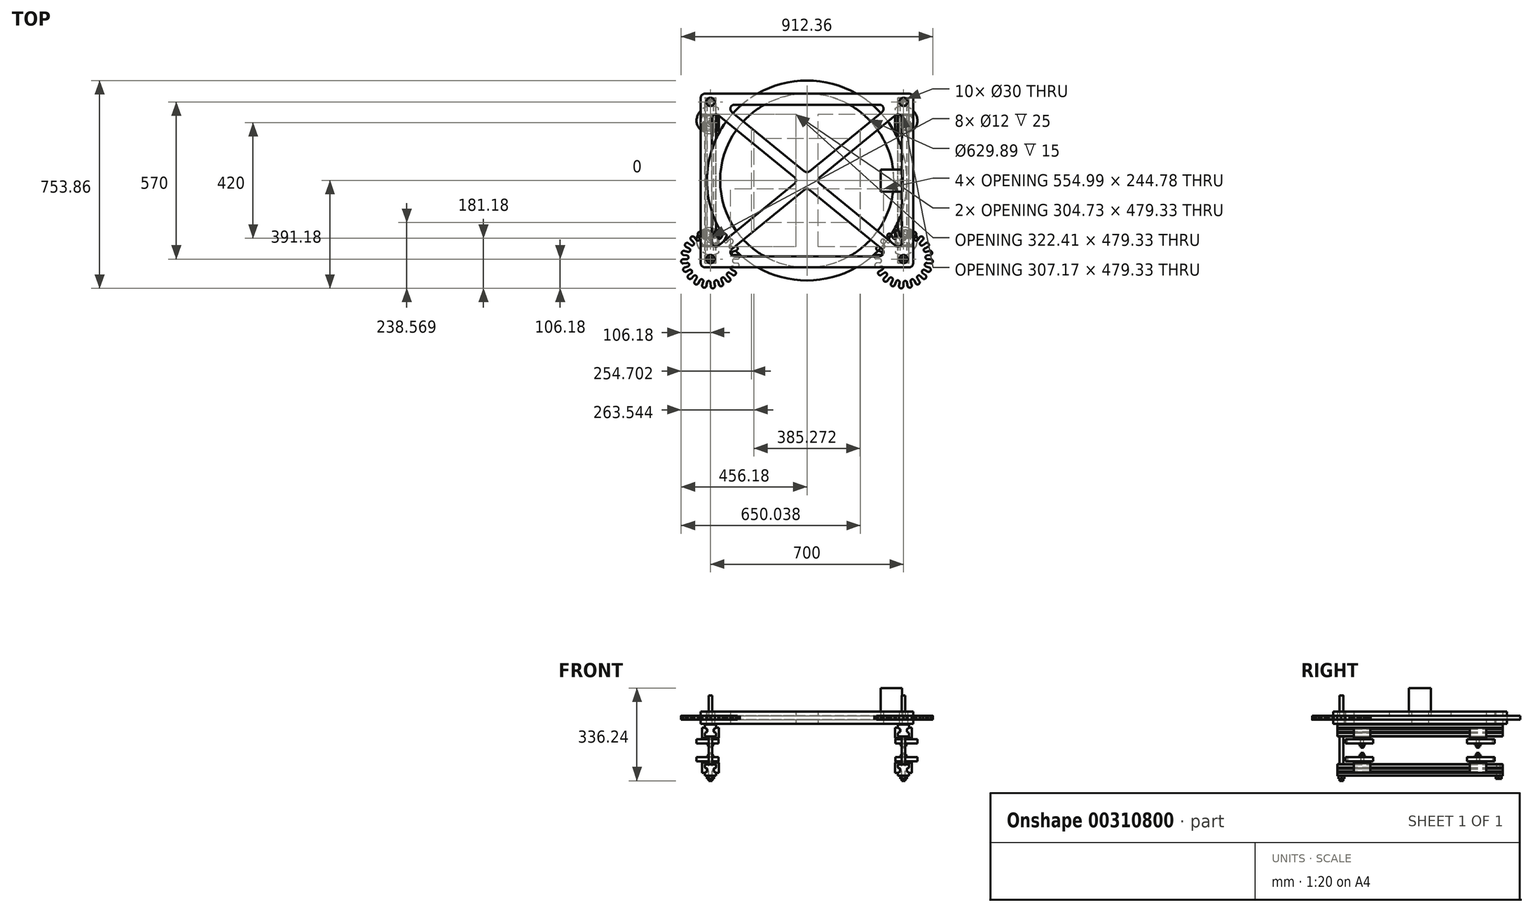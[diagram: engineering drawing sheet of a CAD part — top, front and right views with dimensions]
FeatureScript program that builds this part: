
annotation { "Feature Type Name" : "Feature", "Feature Type Description" : "" }
export const myFeature = defineFeature(function(context is Context, id is Id, definition is map)
    precondition{}
    {
        {
            var Q0;
            Q0=qCreatedBy(makeId("Top.planeOp"),FACE);
            var sketch = newSketch(context, id + "F0", { "sketchPlane" : qUnion([Q0])});
            skLineSegment(sketch, "E0", {"start": v(0, 362.2) * mm, "end": v(0, -359) * mm, "construction": true});
            skLineSegment(sketch, "E1", {"start": v(-350, -300) * mm, "end": v(-350, 300) * mm});
            skLineSegment(sketch, "E2", {"start": v(-645.56, 0) * mm, "end": v(704, 0) * mm, "construction": true});
            skCircle(sketch, "E3", {"center": v(-350, -285) * mm, "radius": 10 * mm});
            skCircle(sketch, "E4.0", {"center": v(-350, -285) * mm, "radius": 6.4 * mm});
            skCircle(sketch, "E5.MirrorC", {"center": v(-350, 285) * mm, "radius": 10 * mm});
            skCircle(sketch, "E6.MirrorC", {"center": v(-350, 285) * mm, "radius": 6.4 * mm});
            skSolve(sketch);
        }
        {
            var Q0;
            Q0=qCreatedBy(makeId("Front.planeOp"),FACE);
            var sketch = newSketch(context, id + "F1", { "sketchPlane" : qUnion([Q0])});
            skPoint(sketch, "E7.0", {"position": v(-350, 0) * mm});
            skLineSegment(sketch, "E8", {"start": v(-350, 0) * mm, "end": v(-330, 0) * mm});
            skLineSegment(sketch, "E9", {"start": v(-330, 0) * mm, "end": v(-330, -12) * mm});
            skLineSegment(sketch, "E10", {"start": v(-330, -12) * mm, "end": v(-338, -16.62) * mm});
            skLineSegment(sketch, "E11", {"start": v(-338, -16.62) * mm, "end": v(-338, -26.62) * mm});
            skLineSegment(sketch, "E12", {"start": v(-338, -26.62) * mm, "end": v(-330, -31.24) * mm});
            skLineSegment(sketch, "E13", {"start": v(-330, -31.24) * mm, "end": v(-330, -41.24) * mm});
            skLineSegment(sketch, "E14", {"start": v(-330, -41.24) * mm, "end": v(-350, -41.24) * mm});
            skLineSegment(sketch, "E15", {"start": v(-350, 0) * mm, "end": v(-350, -46.41) * mm, "construction": true});
            skPoint(sketch, "E16.orphan", {"position": v(-361.17, 0) * mm});
            skLineSegment(sketch, "E17.MirrorCS", {"start": v(-370, -41.24) * mm, "end": v(-350, -41.24) * mm});
            skLineSegment(sketch, "E18.MirrorCS", {"start": v(-370, -31.24) * mm, "end": v(-370, -41.24) * mm});
            skLineSegment(sketch, "E19.MirrorCS", {"start": v(-362, -26.62) * mm, "end": v(-370, -31.24) * mm});
            skLineSegment(sketch, "E20.MirrorCS", {"start": v(-362, -16.62) * mm, "end": v(-362, -26.62) * mm});
            skLineSegment(sketch, "E21.MirrorCS", {"start": v(-370, -12) * mm, "end": v(-362, -16.62) * mm});
            skLineSegment(sketch, "E22.MirrorCS", {"start": v(-370, 0) * mm, "end": v(-370, -12) * mm});
            skLineSegment(sketch, "E23.MirrorCS", {"start": v(-350, 0) * mm, "end": v(-370, 0) * mm});
            skLineSegment(sketch, "E24", {"start": v(0, 0) * mm, "end": v(0, -83.34) * mm, "construction": true});
            skSolve(sketch);
        }
        {
            var Q0;
            Q0 = qSketchRegion(id + "F1", true);
            extrude(context, id + "F2", {"entities" : qUnion([Q0]), "depth" : 600 * mm, "offsetDistance" : 25 * mm, "symmetric" : true});
        }
        {
            var Q0;
            {var subQ0=sQuery(id+"F0.wireOp",EDGE,"E4.0");var subQ1=sQuery(id+"F0.wireOp",EDGE,"E1");var subQ2=makeQuery(id+"F0.imprint","INTERSECT",VERTEX,{"disambiguationData":[OD(0.0)],"derivedFrom":[subQ1,subQ0]});Q0=makeQuery(id+"F0.imprint","IMPRINT",FACE,{"disambiguationData":[TD([[makeQuery(id+"F0.imprint","IMPRINT",EDGE,{"disambiguationData":[TD([[subQ2,-1.0]])],"derivedFrom":subQ1}),1.0]])]});}
            var Q1;
            {var subQ0=sQuery(id+"F0.wireOp",EDGE,"E4.0");var subQ1=sQuery(id+"F0.wireOp",EDGE,"E1");var subQ2=makeQuery(id+"F0.imprint","INTERSECT",VERTEX,{"disambiguationData":[OD(0.0)],"derivedFrom":[subQ1,subQ0]});Q1=makeQuery(id+"F0.imprint","IMPRINT",FACE,{"disambiguationData":[TD([[makeQuery(id+"F0.imprint","IMPRINT",EDGE,{"disambiguationData":[TD([[subQ2,-1.0]])],"derivedFrom":subQ1}),-1.0]])]});}
            var Q2;
            {var subQ0=sQuery(id+"F0.wireOp",EDGE,"E6.MirrorC");var subQ1=sQuery(id+"F0.wireOp",EDGE,"E1");var subQ2=makeQuery(id+"F0.imprint","INTERSECT",VERTEX,{"disambiguationData":[OD(0.0)],"derivedFrom":[subQ1,subQ0]});Q2=makeQuery(id+"F0.imprint","IMPRINT",FACE,{"disambiguationData":[TD([[makeQuery(id+"F0.imprint","IMPRINT",EDGE,{"disambiguationData":[TD([[subQ2,-1.0]])],"derivedFrom":subQ1}),1.0]])]});}
            var Q3;
            {var subQ0=sQuery(id+"F0.wireOp",EDGE,"E6.MirrorC");var subQ1=sQuery(id+"F0.wireOp",EDGE,"E1");var subQ2=makeQuery(id+"F0.imprint","INTERSECT",VERTEX,{"disambiguationData":[OD(0.0)],"derivedFrom":[subQ1,subQ0]});Q3=makeQuery(id+"F0.imprint","IMPRINT",FACE,{"disambiguationData":[TD([[makeQuery(id+"F0.imprint","IMPRINT",EDGE,{"disambiguationData":[TD([[subQ2,-1.0]])],"derivedFrom":subQ1}),-1.0]])]});}
            var Q4;
            {var subQ0=sQuery(id+"F0.wireOp",EDGE,"7edcf58e-238c-42a4-a463-77a39aa3dbbc0.MirrorC");var subQ1=sQuery(id+"F0.wireOp",EDGE,"05d8a813-b1b4-46cf-a819-2d3db73e43fd0.MirrorCS");var subQ2=makeQuery(id+"F0.imprint","INTERSECT",VERTEX,{"disambiguationData":[OD(0.0)],"derivedFrom":[subQ1,subQ0]});Q4=makeQuery(id+"F0.imprint","IMPRINT",FACE,{"disambiguationData":[TD([[makeQuery(id+"F0.imprint","IMPRINT",EDGE,{"disambiguationData":[TD([[subQ2,-1.0]])],"derivedFrom":subQ1}),-1.0]])]});}
            var Q5;
            {var subQ0=sQuery(id+"F0.wireOp",EDGE,"7edcf58e-238c-42a4-a463-77a39aa3dbbc0.MirrorC");var subQ1=sQuery(id+"F0.wireOp",EDGE,"05d8a813-b1b4-46cf-a819-2d3db73e43fd0.MirrorCS");var subQ2=makeQuery(id+"F0.imprint","INTERSECT",VERTEX,{"disambiguationData":[OD(0.0)],"derivedFrom":[subQ1,subQ0]});Q5=makeQuery(id+"F0.imprint","IMPRINT",FACE,{"disambiguationData":[TD([[makeQuery(id+"F0.imprint","IMPRINT",EDGE,{"disambiguationData":[TD([[subQ2,-1.0]])],"derivedFrom":subQ1}),1.0]])]});}
            var Q6;
            {var subQ0=sQuery(id+"F0.wireOp",EDGE,"8badf943-bae0-46a3-bb4d-9388d6aff6ef0.MirrorC");var subQ1=sQuery(id+"F0.wireOp",EDGE,"05d8a813-b1b4-46cf-a819-2d3db73e43fd0.MirrorCS");var subQ2=makeQuery(id+"F0.imprint","INTERSECT",VERTEX,{"disambiguationData":[OD(0.0)],"derivedFrom":[subQ1,subQ0]});Q6=makeQuery(id+"F0.imprint","IMPRINT",FACE,{"disambiguationData":[TD([[makeQuery(id+"F0.imprint","IMPRINT",EDGE,{"disambiguationData":[TD([[subQ2,-1.0]])],"derivedFrom":subQ1}),-1.0]])]});}
            var Q7;
            {var subQ0=sQuery(id+"F0.wireOp",EDGE,"8badf943-bae0-46a3-bb4d-9388d6aff6ef0.MirrorC");var subQ1=sQuery(id+"F0.wireOp",EDGE,"05d8a813-b1b4-46cf-a819-2d3db73e43fd0.MirrorCS");var subQ2=makeQuery(id+"F0.imprint","INTERSECT",VERTEX,{"disambiguationData":[OD(0.0)],"derivedFrom":[subQ1,subQ0]});Q7=makeQuery(id+"F0.imprint","IMPRINT",FACE,{"disambiguationData":[TD([[makeQuery(id+"F0.imprint","IMPRINT",EDGE,{"disambiguationData":[TD([[subQ2,-1.0]])],"derivedFrom":subQ1}),1.0]])]});}
            extrude(context, id + "F3", {"entities" : qUnion([Q0, Q1, Q2, Q3, Q4, Q5, Q6, Q7]), "operationType" : NewBodyOperationType.REMOVE, "endBound" : BoundingType.UP_TO_NEXT, "oppositeDirection" : true, "depth" : 25 * mm, "offsetDistance" : 25 * mm});
        }
        {
            var Q0;
            Q0=makeQuery(id+"F2.opExtrude","CAP_FACE",FACE,{"disambiguationData":[OSD([sQuery(id+"F1.wireOp",EDGE,"E8"),sQuery(id+"F1.wireOp",EDGE,"E9"),sQuery(id+"F1.wireOp",EDGE,"E10"),sQuery(id+"F1.wireOp",EDGE,"E11"),sQuery(id+"F1.wireOp",EDGE,"E12"),sQuery(id+"F1.wireOp",EDGE,"E13"),sQuery(id+"F1.wireOp",EDGE,"E14"),sQuery(id+"F1.wireOp",EDGE,"E17.MirrorCS"),sQuery(id+"F1.wireOp",EDGE,"E18.MirrorCS"),sQuery(id+"F1.wireOp",EDGE,"E19.MirrorCS"),sQuery(id+"F1.wireOp",EDGE,"E20.MirrorCS"),sQuery(id+"F1.wireOp",EDGE,"E21.MirrorCS"),sQuery(id+"F1.wireOp",EDGE,"E22.MirrorCS"),sQuery(id+"F1.wireOp",EDGE,"E23.MirrorCS")])],"isStart":false});
            cPlane(context, id + "F4", {"entities" : qUnion([Q0]), "cplaneType" : CPlaneType.OFFSET, "offset" : 60 * mm, "oppositeDirection" : true, "width" : 150 * mm, "height" : 150 * mm});
        }
        {
            var Q0;
            Q0=qCreatedBy(id+"F4.planeOp",FACE);
            var sketch = newSketch(context, id + "F5", { "sketchPlane" : qUnion([Q0])});
            skLineSegment(sketch, "E25.0.1", {"start": v(-370, 0) * mm, "end": v(-370, -12) * mm, "construction": true});
            skLineSegment(sketch, "E25.0.2", {"start": v(-370, -12) * mm, "end": v(-362, -16.62) * mm, "construction": true});
            skLineSegment(sketch, "E25.0.3", {"start": v(-362, -16.62) * mm, "end": v(-362, -26.62) * mm, "construction": true});
            skLineSegment(sketch, "E25.0.4", {"start": v(-362, -26.62) * mm, "end": v(-370, -31.24) * mm, "construction": true});
            skLineSegment(sketch, "E25.0.5", {"start": v(-370, -31.24) * mm, "end": v(-370, -41.24) * mm, "construction": true});
            skLineSegment(sketch, "E25.0.7", {"start": v(-330, -41.24) * mm, "end": v(-330, -31.24) * mm, "construction": true});
            skLineSegment(sketch, "E25.0.8", {"start": v(-330, -31.24) * mm, "end": v(-338, -26.62) * mm, "construction": true});
            skLineSegment(sketch, "E25.0.9", {"start": v(-338, -26.62) * mm, "end": v(-338, -16.62) * mm, "construction": true});
            skLineSegment(sketch, "E25.0.10", {"start": v(-338, -16.62) * mm, "end": v(-330, -12) * mm, "construction": true});
            skLineSegment(sketch, "E25.0.11", {"start": v(-330, -12) * mm, "end": v(-330, 0) * mm, "construction": true});
            skLineSegment(sketch, "E26.0", {"start": v(-329.5, -12.29) * mm, "end": v(-329.5, 0.5) * mm});
            skLineSegment(sketch, "E26.2", {"start": v(-329, -31.24) * mm, "end": v(-337.5, -26.33) * mm});
            skLineSegment(sketch, "E26.3", {"start": v(-337.5, -26.33) * mm, "end": v(-337.5, -16.9) * mm});
            skLineSegment(sketch, "E26.4", {"start": v(-337.5, -16.9) * mm, "end": v(-329.5, -12.29) * mm});
            skLineSegment(sketch, "E27", {"start": v(-370, 0) * mm, "end": v(-330, 0) * mm, "construction": true});
            skLineSegment(sketch, "E28.1", {"start": v(-362.5, -26.33) * mm, "end": v(-371, -31.24) * mm});
            skLineSegment(sketch, "E28.2", {"start": v(-370.5, 0.5) * mm, "end": v(-329.5, 0.5) * mm});
            skLineSegment(sketch, "E28.3", {"start": v(-370.5, 0.5) * mm, "end": v(-370.5, -12.29) * mm});
            skLineSegment(sketch, "E28.4", {"start": v(-370.5, -12.29) * mm, "end": v(-362.5, -16.9) * mm});
            skLineSegment(sketch, "E28.5", {"start": v(-362.5, -16.9) * mm, "end": v(-362.5, -26.33) * mm});
            skLineSegment(sketch, "E29", {"start": v(-371, -31.24) * mm, "end": v(-380.5, -31.24) * mm});
            skLineSegment(sketch, "E30", {"start": v(-380.5, -31.24) * mm, "end": v(-380.5, 10.5) * mm});
            skLineSegment(sketch, "E31", {"start": v(-319.5, 10.5) * mm, "end": v(-319.5, -31.24) * mm});
            skLineSegment(sketch, "E32", {"start": v(-319.5, -31.24) * mm, "end": v(-329, -31.24) * mm});
            skLineSegment(sketch, "E33", {"start": v(-380.5, 10.5) * mm, "end": v(-319.5, 10.5) * mm});
            skSolve(sketch);
        }
        {
            var Q0;
            Q0 = qSketchRegion(id + "F5", true);
            extrude(context, id + "F6", {"entities" : qUnion([Q0]), "oppositeDirection" : true, "depth" : 60 * mm, "offsetDistance" : 25 * mm});
        }
        {
            var Q0;
            Q0=makeQuery(id+"F2.opExtrude","SWEPT_EDGE",EDGE,{"disambiguationData":[OSD([sQuery(id+"F1.wireOp",EDGE,"E8"),sQuery(id+"F1.wireOp",EDGE,"E9")])]});
            var Q1;
            Q1=makeQuery(id+"F2.opExtrude","SWEPT_FACE",FACE,{"disambiguationData":[OSD([sQuery(id+"F1.wireOp",EDGE,"E8"),sQuery(id+"F1.wireOp",EDGE,"E23.MirrorCS")])]});
            var Q2;
            Q2=makeQuery(id+"F2.opExtrude","SWEPT_EDGE",EDGE,{"disambiguationData":[OSD([sQuery(id+"F1.wireOp",EDGE,"aa46a0b6-513b-4986-81cd-16920383a29b9.MirrorCS"),sQuery(id+"F1.wireOp",EDGE,"aa46a0b6-513b-4986-81cd-16920383a29b11.MirrorCS")])]});
            var Q3;
            Q3=makeQuery(id+"F2.opExtrude","SWEPT_FACE",FACE,{"disambiguationData":[OSD([sQuery(id+"F1.wireOp",EDGE,"aa46a0b6-513b-4986-81cd-16920383a29b10.MirrorCS"),sQuery(id+"F1.wireOp",EDGE,"aa46a0b6-513b-4986-81cd-16920383a29b11.MirrorCS")])]});
            chamfer(context, id + "F7", {"entities" : qUnion([Q0, Q1, Q2, Q3]), "width" : 1 * mm, "tangentPropagation" : true});
        }
        {
            var Q0;
            Q0=makeQuery(id+"F6.opExtrude","SWEPT_EDGE",EDGE,{"disambiguationData":[OSD([sQuery(id+"F5.wireOp",EDGE,"E28.2"),sQuery(id+"F5.wireOp",EDGE,"E28.3")])]});
            var Q1;
            Q1=makeQuery(id+"F6.opExtrude","SWEPT_EDGE",EDGE,{"disambiguationData":[OSD([sQuery(id+"F5.wireOp",EDGE,"E26.0"),sQuery(id+"F5.wireOp",EDGE,"E28.2")])]});
            chamfer(context, id + "F8", {"entities" : qUnion([Q0, Q1]), "width" : 1 * mm, "tangentPropagation" : true});
        }
        {
            var Q0;
            Q0=makeQuery(id+"F6.opExtrude","CAP_EDGE",EDGE,{"disambiguationData":[OSD([sQuery(id+"F5.wireOp",EDGE,"E33")])],"isStart":true});
            var Q1;
            Q1=makeQuery(id+"F6.opExtrude","SWEPT_FACE",FACE,{"disambiguationData":[OSD([sQuery(id+"F5.wireOp",EDGE,"E33")])]});
            chamfer(context, id + "F9", {"entities" : qUnion([Q0, Q1]), "width" : 5 * mm, "tangentPropagation" : true});
        }
        {
            var Q0;
            Q0=makeQuery(id+"F6.opExtrude","SWEPT_FACE",FACE,{"disambiguationData":[OSD([sQuery(id+"F5.wireOp",EDGE,"E33")])]});
            var sketch = newSketch(context, id + "F10", { "sketchPlane" : qUnion([Q0])});
            skCircle(sketch, "E34", {"center": v(-350, -210) * mm, "radius": 5 * mm});
            skPoint(sketch, "E34.centerSnap0", {"position": v(-324.5, -210) * mm});
            skPoint(sketch, "E34.centerSnap1", {"position": v(-350, -235) * mm});
            skCircle(sketch, "E35.0", {"center": v(-350, -210) * mm, "radius": 6 * mm});
            skCircle(sketch, "E36", {"center": v(-350, -210) * mm, "radius": 29 * mm, "construction": true});
            skArc(sketch, "E37", {"start": v(-350, -270) * mm, "mid": v(-335.03, -268.1) * mm, "end": v(-321, -262.53) * mm});
            skLineSegment(sketch, "E38", {"start": v(-350, -270) * mm, "end": v(-350, -150) * mm, "construction": true});
            skLineSegment(sketch, "E39", {"start": v(-321, -210) * mm, "end": v(-410, -210) * mm, "construction": true});
            skFitSpline(sketch, "E40", {"points": [v(-350, -270) * mm, v(-400, -210) * mm, v(-350, -170) * mm, v(-321, -210) * mm], "startDerivative": vector(-250.58, 0) * mm, "endDerivative": vector(0, -219.6) * mm});
            skLineSegment(sketch, "E41", {"start": v(-321, -210) * mm, "end": v(-321, -262.53) * mm});
            skLineSegment(sketch, "E42", {"start": v(-350, -270) * mm, "end": v(-312.43, -270) * mm, "construction": true});
            skSolve(sketch);
        }
        {
            var Q0;
            Q0=makeQuery(id+"F10.imprint","IMPRINT",FACE,{"disambiguationData":[TD([[makeQuery(id+"F10.imprint","IMPRINT",EDGE,{"derivedFrom":sQuery(id+"F10.wireOp",EDGE,"E34")}),1.0]])]});
            var Q1;
            Q1=sQuery(id+"F10.wireOp",EDGE,"E34");
            extrude(context, id + "F11", {"entities" : qUnion([Q0]), "operationType" : NewBodyOperationType.ADD, "surfaceEntities" : qUnion([Q1]), "depth" : 30 * mm, "offsetDistance" : 25 * mm});
        }
        {
            var Q0;
            {var subQ6=sQuery(id+"F10.wireOp",EDGE,"E37");Q0=makeQuery(id+"F10.imprint","IMPRINT",FACE,{"disambiguationData":[TD([[makeQuery(id+"F10.imprint","IMPRINT",EDGE,{"derivedFrom":subQ6}),1.0]])]});}
            var Q1;
            Q1=makeQuery(id+"F10.imprint","IMPRINT",FACE,{"disambiguationData":[TD([[makeQuery(id+"F10.imprint","IMPRINT",EDGE,{"derivedFrom":sQuery(id+"F10.wireOp",EDGE,"E35.0")}),-1.0]])]});
            extrude(context, id + "F12", {"entities" : qUnion([Q0, Q1]), "depth" : 15 * mm, "offsetDistance" : 25 * mm});
        }
        {
            var Q0;
            Q0=makeQuery(id+"F12.opExtrude","CAP_FACE",FACE,{"disambiguationData":[OSD([sQuery(id+"F10.wireOp",EDGE,"E35.0"),sQuery(id+"F10.wireOp",EDGE,"E37"),sQuery(id+"F10.wireOp",EDGE,"E40"),sQuery(id+"F10.wireOp",EDGE,"E41")])],"isStart":false});
            var sketch = newSketch(context, id + "F13", { "sketchPlane" : qUnion([Q0])});
            skCircle(sketch, "E43.0", {"center": v(-350, -210) * mm, "radius": 5 * mm});
            skCircle(sketch, "E44", {"center": v(-350, -210) * mm, "radius": 15 * mm});
            skCircle(sketch, "E45.cCircle", {"center": v(-350, -210) * mm, "radius": 8.06 * mm, "construction": true});
            skLineSegment(sketch, "E45.0", {"start": v(-345.35, -218.06) * mm, "end": v(-354.65, -218.06) * mm});
            skLineSegment(sketch, "E45.1", {"start": v(-354.65, -218.06) * mm, "end": v(-359.3, -210) * mm});
            skLineSegment(sketch, "E45.2", {"start": v(-359.3, -210) * mm, "end": v(-354.65, -201.94) * mm});
            skLineSegment(sketch, "E45.3", {"start": v(-354.65, -201.94) * mm, "end": v(-345.35, -201.94) * mm});
            skLineSegment(sketch, "E45.4", {"start": v(-345.35, -201.94) * mm, "end": v(-340.7, -210) * mm});
            skLineSegment(sketch, "E45.5", {"start": v(-340.7, -210) * mm, "end": v(-345.35, -218.06) * mm});
            skPoint(sketch, "E45.0.midPoint", {"position": v(-350, -218.06) * mm});
            skSolve(sketch);
        }
        {
            var Q0;
            Q0=makeQuery(id+"F13.imprint","IMPRINT",FACE,{"disambiguationData":[TD([[makeQuery(id+"F13.imprint","IMPRINT",EDGE,{"derivedFrom":sQuery(id+"F13.wireOp",EDGE,"E44")}),1.0]])]});
            var Q1;
            Q1=makeQuery(id+"F13.imprint","IMPRINT",FACE,{"disambiguationData":[TD([[makeQuery(id+"F13.imprint","IMPRINT",EDGE,{"derivedFrom":sQuery(id+"F13.wireOp",EDGE,"E45.0")}),-1.0]])]});
            extrude(context, id + "F14", {"entities" : qUnion([Q0, Q1]), "depth" : 2 * mm, "offsetDistance" : 25 * mm});
        }
        {
            var Q0;
            Q0=makeQuery(id+"F13.imprint","IMPRINT",FACE,{"disambiguationData":[TD([[makeQuery(id+"F13.imprint","IMPRINT",EDGE,{"derivedFrom":sQuery(id+"F13.wireOp",EDGE,"E45.0")}),-1.0]])]});
            extrude(context, id + "F15", {"entities" : qUnion([Q0]), "depth" : 10 * mm, "offsetDistance" : 25 * mm});
        }
        {
            var Q0;
            {var subQ0=sQuery(id+"F0.wireOp",EDGE,"E3");var subQ1=sQuery(id+"F0.wireOp",EDGE,"E1");var subQ2=makeQuery(id+"F0.imprint","INTERSECT",VERTEX,{"disambiguationData":[OD(0.0)],"derivedFrom":[subQ1,subQ0]});Q0=makeQuery(id+"F0.imprint","IMPRINT",FACE,{"disambiguationData":[TD([[makeQuery(id+"F0.imprint","IMPRINT",EDGE,{"disambiguationData":[TD([[subQ2,-1.0]])],"derivedFrom":subQ1}),1.0]])]});}
            var Q1;
            {var subQ0=sQuery(id+"F0.wireOp",EDGE,"E3");var subQ1=sQuery(id+"F0.wireOp",EDGE,"E1");var subQ2=makeQuery(id+"F0.imprint","INTERSECT",VERTEX,{"disambiguationData":[OD(0.0)],"derivedFrom":[subQ1,subQ0]});Q1=makeQuery(id+"F0.imprint","IMPRINT",FACE,{"disambiguationData":[TD([[makeQuery(id+"F0.imprint","IMPRINT",EDGE,{"disambiguationData":[TD([[subQ2,-1.0]])],"derivedFrom":subQ1}),-1.0]])]});}
            var Q2;
            {var subQ0=sQuery(id+"F0.wireOp",EDGE,"E4.0");var subQ1=sQuery(id+"F0.wireOp",EDGE,"E1");var subQ2=makeQuery(id+"F0.imprint","INTERSECT",VERTEX,{"disambiguationData":[OD(0.0)],"derivedFrom":[subQ1,subQ0]});Q2=makeQuery(id+"F0.imprint","IMPRINT",FACE,{"disambiguationData":[TD([[makeQuery(id+"F0.imprint","IMPRINT",EDGE,{"disambiguationData":[TD([[subQ2,-1.0]])],"derivedFrom":subQ1}),1.0]])]});}
            var Q3;
            {var subQ0=sQuery(id+"F0.wireOp",EDGE,"E4.0");var subQ1=sQuery(id+"F0.wireOp",EDGE,"E1");var subQ2=makeQuery(id+"F0.imprint","INTERSECT",VERTEX,{"disambiguationData":[OD(0.0)],"derivedFrom":[subQ1,subQ0]});Q3=makeQuery(id+"F0.imprint","IMPRINT",FACE,{"disambiguationData":[TD([[makeQuery(id+"F0.imprint","IMPRINT",EDGE,{"disambiguationData":[TD([[subQ2,-1.0]])],"derivedFrom":subQ1}),-1.0]])]});}
            extrude(context, id + "F16", {"entities" : qUnion([Q0, Q1, Q2, Q3]), "depth" : 250 * mm, "offsetDistance" : 25 * mm});
        }
        {
            var Q0;
            {var subQ0=sQuery(id+"F0.wireOp",EDGE,"E4.0");var subQ1=sQuery(id+"F0.wireOp",EDGE,"E1");var subQ2=makeQuery(id+"F0.imprint","INTERSECT",VERTEX,{"disambiguationData":[OD(0.0)],"derivedFrom":[subQ1,subQ0]});Q0=makeQuery(id+"F0.imprint","IMPRINT",FACE,{"disambiguationData":[TD([[makeQuery(id+"F0.imprint","IMPRINT",EDGE,{"disambiguationData":[TD([[subQ2,-1.0]])],"derivedFrom":subQ1}),1.0]])]});}
            var Q1;
            {var subQ0=sQuery(id+"F0.wireOp",EDGE,"E4.0");var subQ1=sQuery(id+"F0.wireOp",EDGE,"E1");var subQ2=makeQuery(id+"F0.imprint","INTERSECT",VERTEX,{"disambiguationData":[OD(0.0)],"derivedFrom":[subQ1,subQ0]});Q1=makeQuery(id+"F0.imprint","IMPRINT",FACE,{"disambiguationData":[TD([[makeQuery(id+"F0.imprint","IMPRINT",EDGE,{"disambiguationData":[TD([[subQ2,-1.0]])],"derivedFrom":subQ1}),-1.0]])]});}
            extrude(context, id + "F17", {"entities" : qUnion([Q0, Q1]), "operationType" : NewBodyOperationType.ADD, "oppositeDirection" : true, "depth" : 60 * mm, "offsetDistance" : 25 * mm});
        }
        {
            var Q0;
            Q0=makeQuery(id+"F2.opExtrude","SWEPT_FACE",FACE,{"disambiguationData":[OSD([sQuery(id+"F1.wireOp",EDGE,"E14"),sQuery(id+"F1.wireOp",EDGE,"E17.MirrorCS")])]});
            var sketch = newSketch(context, id + "F18", { "sketchPlane" : qUnion([Q0])});
            skCircle(sketch, "E46", {"center": v(-350, 285) * mm, "radius": 15 * mm});
            skCircle(sketch, "E47.cCircle", {"center": v(-350, 285) * mm, "radius": 10.5 * mm, "construction": true});
            skLineSegment(sketch, "E47.0", {"start": v(-356.06, 295.5) * mm, "end": v(-343.94, 295.5) * mm});
            skLineSegment(sketch, "E47.1", {"start": v(-343.94, 295.5) * mm, "end": v(-337.87, 285) * mm});
            skLineSegment(sketch, "E47.2", {"start": v(-337.87, 285) * mm, "end": v(-343.94, 274.5) * mm});
            skLineSegment(sketch, "E47.3", {"start": v(-343.94, 274.5) * mm, "end": v(-356.06, 274.5) * mm});
            skLineSegment(sketch, "E47.4", {"start": v(-356.06, 274.5) * mm, "end": v(-362.13, 285) * mm});
            skLineSegment(sketch, "E47.5", {"start": v(-362.13, 285) * mm, "end": v(-356.06, 295.5) * mm});
            skPoint(sketch, "E47.0.midPoint", {"position": v(-350, 295.5) * mm});
            skSolve(sketch);
        }
        {
            var Q0;
            Q0=makeQuery(id+"F18.imprint","IMPRINT",FACE,{"disambiguationData":[TD([[makeQuery(id+"F18.imprint","IMPRINT",EDGE,{"derivedFrom":sQuery(id+"F18.wireOp",EDGE,"E47.0")}),-1.0]])]});
            extrude(context, id + "F19", {"entities" : qUnion([Q0]), "depth" : 12 * mm, "offsetDistance" : 25 * mm});
        }
        {
            var Q0;
            Q0=makeQuery(id+"F18.imprint","IMPRINT",FACE,{"disambiguationData":[TD([[makeQuery(id+"F18.imprint","IMPRINT",EDGE,{"derivedFrom":sQuery(id+"F18.wireOp",EDGE,"E46")}),1.0]])]});
            extrude(context, id + "F20", {"entities" : qUnion([Q0]), "depth" : 2 * mm, "offsetDistance" : 25 * mm});
        }
        {
            var Q0;
            Q0=makeQuery(id+"F20.opExtrude","SWEPT_BODY",BODY,{"disambiguationData":[OSD([sQuery(id+"F18.wireOp",EDGE,"E46"),sQuery(id+"F18.wireOp",EDGE,"E47.0"),sQuery(id+"F18.wireOp",EDGE,"E47.1"),sQuery(id+"F18.wireOp",EDGE,"E47.2"),sQuery(id+"F18.wireOp",EDGE,"E47.3"),sQuery(id+"F18.wireOp",EDGE,"E47.4"),sQuery(id+"F18.wireOp",EDGE,"E47.5")])]});
            var Q1;
            Q1=makeQuery(id+"F19.opExtrude","SWEPT_BODY",BODY,{"disambiguationData":[OSD([sQuery(id+"F0.wireOp",EDGE,"E4.0"),sQuery(id+"F1.wireOp",EDGE,"E14"),sQuery(id+"F1.wireOp",EDGE,"E17.MirrorCS"),sQuery(id+"F18.wireOp",EDGE,"E47.0"),sQuery(id+"F18.wireOp",EDGE,"E47.1"),sQuery(id+"F18.wireOp",EDGE,"E47.2"),sQuery(id+"F18.wireOp",EDGE,"E47.3"),sQuery(id+"F18.wireOp",EDGE,"E47.4"),sQuery(id+"F18.wireOp",EDGE,"E47.5")])]});
            var Q2;
            Q2=makeQuery(id+"F16.opExtrude","SWEPT_BODY",BODY,{"disambiguationData":[OSD([sQuery(id+"F0.wireOp",EDGE,"E3")])]});
            var Q3;
            Q3=makeQuery(id+"F15.opExtrude","SWEPT_BODY",BODY,{"disambiguationData":[OSD([sQuery(id+"F10.wireOp",EDGE,"E35.0"),sQuery(id+"F13.wireOp",EDGE,"E45.0"),sQuery(id+"F13.wireOp",EDGE,"E45.1"),sQuery(id+"F13.wireOp",EDGE,"E45.2"),sQuery(id+"F13.wireOp",EDGE,"E45.3"),sQuery(id+"F13.wireOp",EDGE,"E45.4"),sQuery(id+"F13.wireOp",EDGE,"E45.5")])]});
            var Q4;
            Q4=makeQuery(id+"F14.opExtrude","SWEPT_BODY",BODY,{"disambiguationData":[OSD([sQuery(id+"F10.wireOp",EDGE,"E35.0"),sQuery(id+"F13.wireOp",EDGE,"E44")])]});
            var Q5;
            Q5=makeQuery(id+"F12.opExtrude","SWEPT_BODY",BODY,{"disambiguationData":[OSD([sQuery(id+"F10.wireOp",EDGE,"E35.0"),sQuery(id+"F10.wireOp",EDGE,"E37"),sQuery(id+"F10.wireOp",EDGE,"E40"),sQuery(id+"F10.wireOp",EDGE,"E41")])]});
            var Q6;
            Q6=makeQuery(id+"F6.opExtrude","SWEPT_BODY",BODY,{"disambiguationData":[OSD([sQuery(id+"F5.wireOp",EDGE,"E26.0"),sQuery(id+"F5.wireOp",EDGE,"E26.2"),sQuery(id+"F5.wireOp",EDGE,"E26.3"),sQuery(id+"F5.wireOp",EDGE,"E26.4"),sQuery(id+"F5.wireOp",EDGE,"E28.1"),sQuery(id+"F5.wireOp",EDGE,"E28.2"),sQuery(id+"F5.wireOp",EDGE,"E28.3"),sQuery(id+"F5.wireOp",EDGE,"E28.4"),sQuery(id+"F5.wireOp",EDGE,"E28.5"),sQuery(id+"F5.wireOp",EDGE,"E29"),sQuery(id+"F5.wireOp",EDGE,"E30"),sQuery(id+"F5.wireOp",EDGE,"E31"),sQuery(id+"F5.wireOp",EDGE,"E32"),sQuery(id+"F5.wireOp",EDGE,"E33")])]});
            var Q7;
            Q7=qCreatedBy(makeId("Front.planeOp"),FACE);
            mirror(context, id + "F21", {"operationType" : NewBodyOperationType.ADD, "entities" : qUnion([Q0, Q1, Q2, Q3, Q4, Q5, Q6]), "mirrorPlane" : qUnion([Q7])});
        }
        {
            var Q0;
            Q0=makeQuery(id+"F6.opExtrude","SWEPT_BODY",BODY,{"disambiguationData":[OSD([sQuery(id+"F5.wireOp",EDGE,"E26.0"),sQuery(id+"F5.wireOp",EDGE,"E26.2"),sQuery(id+"F5.wireOp",EDGE,"E26.3"),sQuery(id+"F5.wireOp",EDGE,"E26.4"),sQuery(id+"F5.wireOp",EDGE,"E28.1"),sQuery(id+"F5.wireOp",EDGE,"E28.2"),sQuery(id+"F5.wireOp",EDGE,"E28.3"),sQuery(id+"F5.wireOp",EDGE,"E28.4"),sQuery(id+"F5.wireOp",EDGE,"E28.5"),sQuery(id+"F5.wireOp",EDGE,"E29"),sQuery(id+"F5.wireOp",EDGE,"E30"),sQuery(id+"F5.wireOp",EDGE,"E31"),sQuery(id+"F5.wireOp",EDGE,"E32"),sQuery(id+"F5.wireOp",EDGE,"E33")])]});
            var Q1;
            Q1=makeQuery(id+"F21.opPattern","COPY",BODY,{"derivedFrom":makeQuery(id+"F6.opExtrude","SWEPT_BODY",BODY,{"disambiguationData":[OSD([sQuery(id+"F5.wireOp",EDGE,"E26.0"),sQuery(id+"F5.wireOp",EDGE,"E26.2"),sQuery(id+"F5.wireOp",EDGE,"E26.3"),sQuery(id+"F5.wireOp",EDGE,"E26.4"),sQuery(id+"F5.wireOp",EDGE,"E28.1"),sQuery(id+"F5.wireOp",EDGE,"E28.2"),sQuery(id+"F5.wireOp",EDGE,"E28.3"),sQuery(id+"F5.wireOp",EDGE,"E28.4"),sQuery(id+"F5.wireOp",EDGE,"E28.5"),sQuery(id+"F5.wireOp",EDGE,"E29"),sQuery(id+"F5.wireOp",EDGE,"E30"),sQuery(id+"F5.wireOp",EDGE,"E31"),sQuery(id+"F5.wireOp",EDGE,"E32"),sQuery(id+"F5.wireOp",EDGE,"E33")])]}),"instanceName":"1"});
            var Q2;
            Q2=qCreatedBy(makeId("Right.planeOp"),FACE);
            mirror(context, id + "F22", {"entities" : qUnion([Q0, Q1]), "mirrorPlane" : qUnion([Q2])});
        }
        {
            var Q0;
            Q0=makeQuery(id+"F22.opPattern","COPY",BODY,{"derivedFrom":makeQuery(id+"F21.opPattern","COPY",BODY,{"derivedFrom":makeQuery(id+"F6.opExtrude","SWEPT_BODY",BODY,{"disambiguationData":[OSD([sQuery(id+"F5.wireOp",EDGE,"E26.0"),sQuery(id+"F5.wireOp",EDGE,"E26.2"),sQuery(id+"F5.wireOp",EDGE,"E26.3"),sQuery(id+"F5.wireOp",EDGE,"E26.4"),sQuery(id+"F5.wireOp",EDGE,"E28.1"),sQuery(id+"F5.wireOp",EDGE,"E28.2"),sQuery(id+"F5.wireOp",EDGE,"E28.3"),sQuery(id+"F5.wireOp",EDGE,"E28.4"),sQuery(id+"F5.wireOp",EDGE,"E28.5"),sQuery(id+"F5.wireOp",EDGE,"E29"),sQuery(id+"F5.wireOp",EDGE,"E30"),sQuery(id+"F5.wireOp",EDGE,"E31"),sQuery(id+"F5.wireOp",EDGE,"E32"),sQuery(id+"F5.wireOp",EDGE,"E33")])]}),"instanceName":"1"}),"instanceName":"1"});
            var Q1;
            Q1=makeQuery(id+"F22.opPattern","COPY",BODY,{"derivedFrom":makeQuery(id+"F6.opExtrude","SWEPT_BODY",BODY,{"disambiguationData":[OSD([sQuery(id+"F5.wireOp",EDGE,"E26.0"),sQuery(id+"F5.wireOp",EDGE,"E26.2"),sQuery(id+"F5.wireOp",EDGE,"E26.3"),sQuery(id+"F5.wireOp",EDGE,"E26.4"),sQuery(id+"F5.wireOp",EDGE,"E28.1"),sQuery(id+"F5.wireOp",EDGE,"E28.2"),sQuery(id+"F5.wireOp",EDGE,"E28.3"),sQuery(id+"F5.wireOp",EDGE,"E28.4"),sQuery(id+"F5.wireOp",EDGE,"E28.5"),sQuery(id+"F5.wireOp",EDGE,"E29"),sQuery(id+"F5.wireOp",EDGE,"E30"),sQuery(id+"F5.wireOp",EDGE,"E31"),sQuery(id+"F5.wireOp",EDGE,"E32"),sQuery(id+"F5.wireOp",EDGE,"E33")])]}),"instanceName":"1"});
            deleteBodies(context, id + "F23", {"entities" : qUnion([Q0, Q1])});
        }
        {
            var Q0;
            Q0=makeQuery(id+"F21.opPattern","COPY",BODY,{"derivedFrom":makeQuery(id+"F6.opExtrude","SWEPT_BODY",BODY,{"disambiguationData":[OSD([sQuery(id+"F5.wireOp",EDGE,"E26.0"),sQuery(id+"F5.wireOp",EDGE,"E26.2"),sQuery(id+"F5.wireOp",EDGE,"E26.3"),sQuery(id+"F5.wireOp",EDGE,"E26.4"),sQuery(id+"F5.wireOp",EDGE,"E28.1"),sQuery(id+"F5.wireOp",EDGE,"E28.2"),sQuery(id+"F5.wireOp",EDGE,"E28.3"),sQuery(id+"F5.wireOp",EDGE,"E28.4"),sQuery(id+"F5.wireOp",EDGE,"E28.5"),sQuery(id+"F5.wireOp",EDGE,"E29"),sQuery(id+"F5.wireOp",EDGE,"E30"),sQuery(id+"F5.wireOp",EDGE,"E31"),sQuery(id+"F5.wireOp",EDGE,"E32"),sQuery(id+"F5.wireOp",EDGE,"E33")])]}),"instanceName":"1"});
            var Q1;
            Q1=makeQuery(id+"F6.opExtrude","SWEPT_BODY",BODY,{"disambiguationData":[OSD([sQuery(id+"F5.wireOp",EDGE,"E26.0"),sQuery(id+"F5.wireOp",EDGE,"E26.2"),sQuery(id+"F5.wireOp",EDGE,"E26.3"),sQuery(id+"F5.wireOp",EDGE,"E26.4"),sQuery(id+"F5.wireOp",EDGE,"E28.1"),sQuery(id+"F5.wireOp",EDGE,"E28.2"),sQuery(id+"F5.wireOp",EDGE,"E28.3"),sQuery(id+"F5.wireOp",EDGE,"E28.4"),sQuery(id+"F5.wireOp",EDGE,"E28.5"),sQuery(id+"F5.wireOp",EDGE,"E29"),sQuery(id+"F5.wireOp",EDGE,"E30"),sQuery(id+"F5.wireOp",EDGE,"E31"),sQuery(id+"F5.wireOp",EDGE,"E32"),sQuery(id+"F5.wireOp",EDGE,"E33")])]});
            var Q2;
            Q2=makeQuery(id+"F2.opExtrude","SWEPT_BODY",BODY,{"disambiguationData":[OSD([sQuery(id+"F1.wireOp",EDGE,"E8"),sQuery(id+"F1.wireOp",EDGE,"E9"),sQuery(id+"F1.wireOp",EDGE,"E10"),sQuery(id+"F1.wireOp",EDGE,"E11"),sQuery(id+"F1.wireOp",EDGE,"E12"),sQuery(id+"F1.wireOp",EDGE,"E13"),sQuery(id+"F1.wireOp",EDGE,"E14"),sQuery(id+"F1.wireOp",EDGE,"E17.MirrorCS"),sQuery(id+"F1.wireOp",EDGE,"E18.MirrorCS"),sQuery(id+"F1.wireOp",EDGE,"E19.MirrorCS"),sQuery(id+"F1.wireOp",EDGE,"E20.MirrorCS"),sQuery(id+"F1.wireOp",EDGE,"E21.MirrorCS"),sQuery(id+"F1.wireOp",EDGE,"E22.MirrorCS"),sQuery(id+"F1.wireOp",EDGE,"E23.MirrorCS")])]});
            var Q3;
            Q3=qCreatedBy(makeId("Right.planeOp"),FACE);
            mirror(context, id + "F24", {"entities" : qUnion([Q0, Q1, Q2]), "mirrorPlane" : qUnion([Q3])});
        }
        {
            var Q0;
            Q0=makeQuery(id+"F11.opExtrude","CAP_FACE",FACE,{"disambiguationData":[OSD([sQuery(id+"F10.wireOp",EDGE,"E34")])],"isStart":false});
            cPlane(context, id + "F25", {"entities" : qUnion([Q0]), "cplaneType" : CPlaneType.OFFSET, "offset" : 20 * mm, "width" : 150 * mm, "height" : 150 * mm});
        }
        {
            var Q0;
            Q0=qCreatedBy(id+"F25.planeOp",FACE);
            var sketch = newSketch(context, id + "F26", { "sketchPlane" : qUnion([Q0])});
            skFitSpline(sketch, "E48.0.0", {"points": [v(-321, -210) * mm, v(-321, -188.44) * mm, v(-346.25, -152.42) * mm, v(-425.44, -205.93) * mm, v(-380.93, -270) * mm, v(-350, -270) * mm]});
            skArc(sketch, "E48.0.1", {"start": v(-350, -270) * mm, "mid": v(-335.03, -268.1) * mm, "end": v(-321, -262.53) * mm});
            skLineSegment(sketch, "E48.0.2", {"start": v(-321, -262.53) * mm, "end": v(-321, -210) * mm});
            skFitSpline(sketch, "E49.0.0", {"points": [v(-350, 270) * mm, v(-380.93, 270) * mm, v(-425.44, 205.93) * mm, v(-346.25, 152.42) * mm, v(-321, 188.44) * mm, v(-321, 210) * mm]});
            skLineSegment(sketch, "E49.0.1", {"start": v(-321, 210) * mm, "end": v(-321, 262.53) * mm});
            skArc(sketch, "E49.0.2", {"start": v(-321, 262.53) * mm, "mid": v(-335.03, 268.1) * mm, "end": v(-350, 270) * mm});
            skFitSpline(sketch, "E50.0.0", {"points": [v(350, -270) * mm, v(380.93, -270) * mm, v(425.44, -205.93) * mm, v(346.25, -152.42) * mm, v(321, -188.44) * mm, v(321, -210) * mm]});
            skLineSegment(sketch, "E50.0.1", {"start": v(321, -210) * mm, "end": v(321, -262.53) * mm});
            skArc(sketch, "E50.0.2", {"start": v(321, -262.53) * mm, "mid": v(335.03, -268.1) * mm, "end": v(350, -270) * mm});
            skFitSpline(sketch, "E51.0.0", {"points": [v(321, 210) * mm, v(321, 188.44) * mm, v(346.25, 152.42) * mm, v(425.44, 205.93) * mm, v(380.93, 270) * mm, v(350, 270) * mm]});
            skArc(sketch, "E51.0.1", {"start": v(350, 270) * mm, "mid": v(335.03, 268.1) * mm, "end": v(321, 262.53) * mm});
            skLineSegment(sketch, "E51.0.2", {"start": v(321, 262.53) * mm, "end": v(321, 210) * mm});
            skSolve(sketch);
        }
        {
            var Q0;
            Q0=makeQuery(id+"F12.opExtrude","CAP_FACE",FACE,{"disambiguationData":[OSD([sQuery(id+"F10.wireOp",EDGE,"E35.0"),sQuery(id+"F10.wireOp",EDGE,"E37"),sQuery(id+"F10.wireOp",EDGE,"E40"),sQuery(id+"F10.wireOp",EDGE,"E41")])],"isStart":false});
            cPlane(context, id + "F27", {"entities" : qUnion([Q0]), "cplaneType" : CPlaneType.OFFSET, "offset" : 25 * mm, "width" : 150 * mm, "height" : 150 * mm});
        }
        {
            var Q0;
            Q0=makeQuery(id+"F6.opExtrude","SWEPT_BODY",BODY,{"disambiguationData":[OSD([sQuery(id+"F5.wireOp",EDGE,"E26.0"),sQuery(id+"F5.wireOp",EDGE,"E26.2"),sQuery(id+"F5.wireOp",EDGE,"E26.3"),sQuery(id+"F5.wireOp",EDGE,"E26.4"),sQuery(id+"F5.wireOp",EDGE,"E28.1"),sQuery(id+"F5.wireOp",EDGE,"E28.2"),sQuery(id+"F5.wireOp",EDGE,"E28.3"),sQuery(id+"F5.wireOp",EDGE,"E28.4"),sQuery(id+"F5.wireOp",EDGE,"E28.5"),sQuery(id+"F5.wireOp",EDGE,"E29"),sQuery(id+"F5.wireOp",EDGE,"E30"),sQuery(id+"F5.wireOp",EDGE,"E31"),sQuery(id+"F5.wireOp",EDGE,"E32"),sQuery(id+"F5.wireOp",EDGE,"E33")])]});
            var Q1;
            Q1=makeQuery(id+"F21.opPattern","COPY",BODY,{"derivedFrom":makeQuery(id+"F6.opExtrude","SWEPT_BODY",BODY,{"disambiguationData":[OSD([sQuery(id+"F5.wireOp",EDGE,"E26.0"),sQuery(id+"F5.wireOp",EDGE,"E26.2"),sQuery(id+"F5.wireOp",EDGE,"E26.3"),sQuery(id+"F5.wireOp",EDGE,"E26.4"),sQuery(id+"F5.wireOp",EDGE,"E28.1"),sQuery(id+"F5.wireOp",EDGE,"E28.2"),sQuery(id+"F5.wireOp",EDGE,"E28.3"),sQuery(id+"F5.wireOp",EDGE,"E28.4"),sQuery(id+"F5.wireOp",EDGE,"E28.5"),sQuery(id+"F5.wireOp",EDGE,"E29"),sQuery(id+"F5.wireOp",EDGE,"E30"),sQuery(id+"F5.wireOp",EDGE,"E31"),sQuery(id+"F5.wireOp",EDGE,"E32"),sQuery(id+"F5.wireOp",EDGE,"E33")])]}),"instanceName":"1"});
            var Q2;
            Q2=makeQuery(id+"F24.opPattern","COPY",BODY,{"derivedFrom":makeQuery(id+"F6.opExtrude","SWEPT_BODY",BODY,{"disambiguationData":[OSD([sQuery(id+"F5.wireOp",EDGE,"E26.0"),sQuery(id+"F5.wireOp",EDGE,"E26.2"),sQuery(id+"F5.wireOp",EDGE,"E26.3"),sQuery(id+"F5.wireOp",EDGE,"E26.4"),sQuery(id+"F5.wireOp",EDGE,"E28.1"),sQuery(id+"F5.wireOp",EDGE,"E28.2"),sQuery(id+"F5.wireOp",EDGE,"E28.3"),sQuery(id+"F5.wireOp",EDGE,"E28.4"),sQuery(id+"F5.wireOp",EDGE,"E28.5"),sQuery(id+"F5.wireOp",EDGE,"E29"),sQuery(id+"F5.wireOp",EDGE,"E30"),sQuery(id+"F5.wireOp",EDGE,"E31"),sQuery(id+"F5.wireOp",EDGE,"E32"),sQuery(id+"F5.wireOp",EDGE,"E33")])]}),"instanceName":"1"});
            var Q3;
            Q3=makeQuery(id+"F24.opPattern","COPY",BODY,{"derivedFrom":makeQuery(id+"F21.opPattern","COPY",BODY,{"derivedFrom":makeQuery(id+"F6.opExtrude","SWEPT_BODY",BODY,{"disambiguationData":[OSD([sQuery(id+"F5.wireOp",EDGE,"E26.0"),sQuery(id+"F5.wireOp",EDGE,"E26.2"),sQuery(id+"F5.wireOp",EDGE,"E26.3"),sQuery(id+"F5.wireOp",EDGE,"E26.4"),sQuery(id+"F5.wireOp",EDGE,"E28.1"),sQuery(id+"F5.wireOp",EDGE,"E28.2"),sQuery(id+"F5.wireOp",EDGE,"E28.3"),sQuery(id+"F5.wireOp",EDGE,"E28.4"),sQuery(id+"F5.wireOp",EDGE,"E28.5"),sQuery(id+"F5.wireOp",EDGE,"E29"),sQuery(id+"F5.wireOp",EDGE,"E30"),sQuery(id+"F5.wireOp",EDGE,"E31"),sQuery(id+"F5.wireOp",EDGE,"E32"),sQuery(id+"F5.wireOp",EDGE,"E33")])]}),"instanceName":"1"}),"instanceName":"1"});
            var Q4;
            Q4=qCreatedBy(id+"F27.planeOp",FACE);
            mirror(context, id + "F28", {"entities" : qUnion([Q0, Q1, Q2, Q3]), "mirrorPlane" : qUnion([Q4])});
        }
        {
            var Q0;
            Q0=qCreatedBy(makeId("Front.planeOp"),FACE);
            var sketch = newSketch(context, id + "F29", { "sketchPlane" : qUnion([Q0])});
            skLineSegment(sketch, "E52.0", {"start": v(-329.5, 131.95) * mm, "end": v(-337.5, 127.33) * mm, "construction": true});
            skLineSegment(sketch, "E53.0", {"start": v(-337.5, 127.33) * mm, "end": v(-337.5, 117.9) * mm, "construction": true});
            skLineSegment(sketch, "E54.0", {"start": v(-337.5, 117.9) * mm, "end": v(-329.5, 113.29) * mm, "construction": true});
            skLineSegment(sketch, "E55.0", {"start": v(-329.5, 113.29) * mm, "end": v(-329.5, 101.5) * mm, "construction": true});
            skLineSegment(sketch, "E56.0", {"start": v(-329.5, 101.5) * mm, "end": v(-330.5, 100.5) * mm, "construction": true});
            skLineSegment(sketch, "E57.0", {"start": v(-369.5, 100.5) * mm, "end": v(-330.5, 100.5) * mm, "construction": true});
            skLineSegment(sketch, "E58.0", {"start": v(-369.5, 100.5) * mm, "end": v(-370.5, 101.5) * mm, "construction": true});
            skLineSegment(sketch, "E59.0", {"start": v(-370.5, 101.5) * mm, "end": v(-370.5, 113.29) * mm, "construction": true});
            skLineSegment(sketch, "E60.0", {"start": v(-370.5, 113.29) * mm, "end": v(-362.5, 117.9) * mm, "construction": true});
            skLineSegment(sketch, "E61.0", {"start": v(-362.5, 117.9) * mm, "end": v(-362.5, 127.33) * mm, "construction": true});
            skLineSegment(sketch, "E62.0", {"start": v(-362.5, 127.33) * mm, "end": v(-370.5, 131.95) * mm, "construction": true});
            skLineSegment(sketch, "E63", {"start": v(-362.5, 122.62) * mm, "end": v(-337.5, 122.62) * mm, "construction": true});
            skLineSegment(sketch, "E64.MirrorCS", {"start": v(-370.5, 144.74) * mm, "end": v(-329.5, 144.74) * mm, "construction": true});
            skLineSegment(sketch, "E65.MirrorCS", {"start": v(-370.5, 144.74) * mm, "end": v(-370.5, 131.95) * mm, "construction": true});
            skLineSegment(sketch, "E66.MirrorCS", {"start": v(-329.5, 131.95) * mm, "end": v(-329.5, 144.74) * mm, "construction": true});
            skLineSegment(sketch, "E67.0", {"start": v(-369.3, 101) * mm, "end": v(-370, 101.7) * mm});
            skLineSegment(sketch, "E67.1", {"start": v(-370, 101.7) * mm, "end": v(-370, 113) * mm});
            skLineSegment(sketch, "E67.2", {"start": v(-370, 113) * mm, "end": v(-362, 117.62) * mm});
            skLineSegment(sketch, "E67.3", {"start": v(-338, 127.62) * mm, "end": v(-338, 117.62) * mm});
            skLineSegment(sketch, "E67.4", {"start": v(-338, 117.62) * mm, "end": v(-330, 113) * mm});
            skLineSegment(sketch, "E67.5", {"start": v(-330, 113) * mm, "end": v(-330, 101.7) * mm});
            skLineSegment(sketch, "E67.6", {"start": v(-330, 101.7) * mm, "end": v(-330.7, 101) * mm});
            skLineSegment(sketch, "E67.7", {"start": v(-330, 132.24) * mm, "end": v(-338, 127.62) * mm});
            skLineSegment(sketch, "E67.8", {"start": v(-330, 132.24) * mm, "end": v(-330, 144.24) * mm});
            skLineSegment(sketch, "E67.9", {"start": v(-370, 144.24) * mm, "end": v(-330, 144.24) * mm});
            skLineSegment(sketch, "E67.10", {"start": v(-369.3, 101) * mm, "end": v(-330.7, 101) * mm});
            skLineSegment(sketch, "E67.11", {"start": v(-370, 144.24) * mm, "end": v(-370, 132.24) * mm});
            skLineSegment(sketch, "E67.12", {"start": v(-362, 127.62) * mm, "end": v(-370, 132.24) * mm});
            skLineSegment(sketch, "E67.13", {"start": v(-362, 117.62) * mm, "end": v(-362, 127.62) * mm});
            skSolve(sketch);
        }
        {
            var Q0;
            Q0 = qSketchRegion(id + "F29", true);
            extrude(context, id + "F30", {"entities" : qUnion([Q0]), "depth" : 600 * mm, "offsetDistance" : 25 * mm, "symmetric" : true});
        }
        {
            var Q0;
            Q0=makeQuery(id+"F30.opExtrude","SWEPT_BODY",BODY,{"disambiguationData":[OSD([sQuery(id+"F29.wireOp",EDGE,"E67.0"),sQuery(id+"F29.wireOp",EDGE,"E67.1"),sQuery(id+"F29.wireOp",EDGE,"E67.2"),sQuery(id+"F29.wireOp",EDGE,"E67.3"),sQuery(id+"F29.wireOp",EDGE,"E67.4"),sQuery(id+"F29.wireOp",EDGE,"E67.5"),sQuery(id+"F29.wireOp",EDGE,"E67.6"),sQuery(id+"F29.wireOp",EDGE,"E67.7"),sQuery(id+"F29.wireOp",EDGE,"E67.8"),sQuery(id+"F29.wireOp",EDGE,"E67.9"),sQuery(id+"F29.wireOp",EDGE,"E67.10"),sQuery(id+"F29.wireOp",EDGE,"E67.11"),sQuery(id+"F29.wireOp",EDGE,"E67.12"),sQuery(id+"F29.wireOp",EDGE,"E67.13")])]});
            var Q1;
            Q1=qCreatedBy(makeId("Right.planeOp"),FACE);
            mirror(context, id + "F31", {"operationType" : NewBodyOperationType.ADD, "entities" : qUnion([Q0]), "mirrorPlane" : qUnion([Q1])});
        }
        {
            var Q0;
            Q0=makeQuery(id+"Fm1DxXtoiKohCYF_3.opExtrude","CAP_FACE",FACE,{"disambiguationData":[OSD([sQuery(id+"F26.wireOp",EDGE,"E51.0.0"),sQuery(id+"F26.wireOp",EDGE,"E51.0.1"),sQuery(id+"F26.wireOp",EDGE,"E51.0.2")])],"isStart":false});
            var Q1;
            Q1=makeQuery(id+"F30.opExtrude","SWEPT_FACE",FACE,{"disambiguationData":[OSD([sQuery(id+"F29.wireOp",EDGE,"E67.9")])]});
            cPlane(context, id + "F32", {"entities" : qUnion([Q0, Q1]), "cplaneType" : CPlaneType.OFFSET, "offset" : 2 * mm, "width" : 150 * mm, "height" : 150 * mm});
        }
        {
            var Q0;
            Q0=qCreatedBy(id+"F32.planeOp",FACE);
            var sketch = newSketch(context, id + "F33", { "sketchPlane" : qUnion([Q0])});
            skPoint(sketch, "E68.0", {"position": v(370, 300) * mm});
            skLineSegment(sketch, "E69.0", {"start": v(370, 300) * mm, "end": v(330, 300) * mm, "construction": true});
            skCircle(sketch, "E70.0", {"center": v(350, 285) * mm, "radius": 10 * mm, "construction": true});
            skPoint(sketch, "E71.0", {"position": v(-370, -300) * mm});
            skCircle(sketch, "E72.0", {"center": v(-350, -285) * mm, "radius": 10 * mm, "construction": true});
            skCircle(sketch, "E73.0", {"center": v(350, -285) * mm, "radius": 10 * mm, "construction": true});
            skCircle(sketch, "E74.0", {"center": v(-350, 285) * mm, "radius": 10 * mm, "construction": true});
            skLineSegment(sketch, "E75.bottom", {"start": v(-370, -300) * mm, "end": v(370, -300) * mm, "construction": true});
            skLineSegment(sketch, "E75.top", {"start": v(-370, 300) * mm, "end": v(370, 300) * mm, "construction": true});
            skLineSegment(sketch, "E75.left", {"start": v(-370, -300) * mm, "end": v(-370, 300) * mm, "construction": true});
            skLineSegment(sketch, "E75.right", {"start": v(370, -300) * mm, "end": v(370, 300) * mm, "construction": true});
            skLineSegment(sketch, "E76.0", {"start": v(-370, 315) * mm, "end": v(370, 315) * mm});
            skLineSegment(sketch, "E76.1", {"start": v(-385, -300) * mm, "end": v(-385, 300) * mm});
            skLineSegment(sketch, "E76.2", {"start": v(-370, -315) * mm, "end": v(370, -315) * mm});
            skLineSegment(sketch, "E76.3", {"start": v(385, -300) * mm, "end": v(385, 300) * mm});
            skCircle(sketch, "E77.0", {"center": v(350, 285) * mm, "radius": 15 * mm});
            skCircle(sketch, "E78.0", {"center": v(-350, 285) * mm, "radius": 15 * mm});
            skCircle(sketch, "E79.0", {"center": v(-350, -285) * mm, "radius": 15 * mm});
            skCircle(sketch, "E80.0", {"center": v(350, -285) * mm, "radius": 15 * mm});
            skPoint(sketch, "E81.visualSharp", {"position": v(385, -315) * mm});
            skArc(sketch, "E81.filletArc", {"start": v(370, -315) * mm, "mid": v(380.6, -310.6) * mm, "end": v(385, -300) * mm});
            skPoint(sketch, "E82.visualSharp", {"position": v(385, 315) * mm});
            skArc(sketch, "E82.filletArc", {"start": v(385, 300) * mm, "mid": v(380.6, 310.6) * mm, "end": v(370, 315) * mm});
            skPoint(sketch, "E83.visualSharp", {"position": v(-385, 315) * mm});
            skArc(sketch, "E83.filletArc", {"start": v(-370, 315) * mm, "mid": v(-380.6, 310.6) * mm, "end": v(-385, 300) * mm});
            skPoint(sketch, "E84.visualSharp", {"position": v(-385, -315) * mm});
            skArc(sketch, "E84.filletArc", {"start": v(-385, -300) * mm, "mid": v(-380.6, -310.6) * mm, "end": v(-370, -315) * mm});
            skLineSegment(sketch, "E85", {"start": v(-385, -315) * mm, "end": v(385, 315) * mm, "construction": true});
            skLineSegment(sketch, "E86", {"start": v(385, -315) * mm, "end": v(-385, 315) * mm, "construction": true});
            skLineSegment(sketch, "E87.0", {"start": v(320.5, -236.39) * mm, "end": v(45.77, -11.6) * mm});
            skLineSegment(sketch, "E88.0", {"start": v(-272, -248.4) * mm, "end": v(-9.5, -33.61) * mm});
            skLineSegment(sketch, "E89.0", {"start": v(-320.5, -236.39) * mm, "end": v(-45.77, -11.6) * mm});
            skLineSegment(sketch, "E90.trimOffspring", {"start": v(9.5, 33.61) * mm, "end": v(272, 248.4) * mm});
            skLineSegment(sketch, "E91.trimOffspring", {"start": v(-45.77, 11.6) * mm, "end": v(-320.5, 236.39) * mm});
            skLineSegment(sketch, "E92.trimOffspring", {"start": v(-9.5, 33.61) * mm, "end": v(-272, 248.4) * mm});
            skLineSegment(sketch, "E93.trimOffspring", {"start": v(45.77, 11.6) * mm, "end": v(320.5, 236.39) * mm});
            skLineSegment(sketch, "E94.trimOffspring", {"start": v(272, -248.4) * mm, "end": v(9.5, -33.61) * mm});
            skLineSegment(sketch, "E95.2", {"start": v(345, -224.78) * mm, "end": v(345, 224.78) * mm});
            skLineSegment(sketch, "E96.trimOffspring", {"start": v(-262.5, -275) * mm, "end": v(262.5, -275) * mm});
            skLineSegment(sketch, "E97.trimOffspring", {"start": v(-345, -224.78) * mm, "end": v(-345, 224.78) * mm});
            skLineSegment(sketch, "E98.trimOffspring", {"start": v(-262.5, 275) * mm, "end": v(262.5, 275) * mm});
            skPoint(sketch, "E99.visualSharp", {"position": v(345, -256.43) * mm});
            skArc(sketch, "E99.filletArc", {"start": v(320.5, -236.39) * mm, "mid": v(336.42, -238.33) * mm, "end": v(345, -224.78) * mm});
            skPoint(sketch, "E100.visualSharp", {"position": v(304.53, -275) * mm});
            skArc(sketch, "E100.filletArc", {"start": v(262.5, -275) * mm, "mid": v(276.63, -265.04) * mm, "end": v(272, -248.4) * mm});
            skPoint(sketch, "E101.visualSharp", {"position": v(345, 256.43) * mm});
            skArc(sketch, "E101.filletArc", {"start": v(345, 224.78) * mm, "mid": v(336.42, 238.33) * mm, "end": v(320.5, 236.39) * mm});
            skPoint(sketch, "E102.visualSharp", {"position": v(304.53, 275) * mm});
            skArc(sketch, "E102.filletArc", {"start": v(272, 248.4) * mm, "mid": v(276.63, 265.04) * mm, "end": v(262.5, 275) * mm});
            skPoint(sketch, "E103.visualSharp", {"position": v(-304.53, 275) * mm});
            skArc(sketch, "E103.filletArc", {"start": v(-262.5, 275) * mm, "mid": v(-276.63, 265.04) * mm, "end": v(-272, 248.4) * mm});
            skPoint(sketch, "E104.visualSharp", {"position": v(-345, 256.43) * mm});
            skArc(sketch, "E104.filletArc", {"start": v(-320.5, 236.39) * mm, "mid": v(-336.42, 238.33) * mm, "end": v(-345, 224.78) * mm});
            skPoint(sketch, "E105.visualSharp", {"position": v(-345, -256.43) * mm});
            skArc(sketch, "E105.filletArc", {"start": v(-345, -224.78) * mm, "mid": v(-336.42, -238.33) * mm, "end": v(-320.5, -236.39) * mm});
            skPoint(sketch, "E106.visualSharp", {"position": v(-304.53, -275) * mm});
            skArc(sketch, "E106.filletArc", {"start": v(-272, -248.4) * mm, "mid": v(-276.63, -265.04) * mm, "end": v(-262.5, -275) * mm});
            skPoint(sketch, "E107.visualSharp", {"position": v(0, -25.84) * mm});
            skArc(sketch, "E107.filletArc", {"start": v(9.5, -33.61) * mm, "mid": v(0, -30.22) * mm, "end": v(-9.5, -33.61) * mm});
            skPoint(sketch, "E108.visualSharp", {"position": v(-31.58, 0) * mm});
            skArc(sketch, "E108.filletArc", {"start": v(-45.77, -11.6) * mm, "mid": v(-40.27, 0) * mm, "end": v(-45.77, 11.6) * mm});
            skPoint(sketch, "E109.visualSharp", {"position": v(0, 25.84) * mm});
            skArc(sketch, "E109.filletArc", {"start": v(-9.5, 33.61) * mm, "mid": v(0, 30.22) * mm, "end": v(9.5, 33.61) * mm});
            skPoint(sketch, "E110.visualSharp", {"position": v(31.58, 0) * mm});
            skArc(sketch, "E110.filletArc", {"start": v(45.77, 11.6) * mm, "mid": v(40.27, 0) * mm, "end": v(45.77, -11.6) * mm});
            skSolve(sketch);
        }
        {
            var Q0;
            Q0 = qSketchRegion(id + "F33", true);
            extrude(context, id + "F34", {"entities" : qUnion([Q0]), "depth" : 15 * mm, "offsetDistance" : 25 * mm});
        }
        {
            var Q0;
            Q0=makeQuery(id+"F34.opExtrude","CAP_FACE",FACE,{"disambiguationData":[OSD([sQuery(id+"F33.wireOp",EDGE,"E76.0"),sQuery(id+"F33.wireOp",EDGE,"E76.1"),sQuery(id+"F33.wireOp",EDGE,"E76.2"),sQuery(id+"F33.wireOp",EDGE,"E76.3"),sQuery(id+"F33.wireOp",EDGE,"E77.0"),sQuery(id+"F33.wireOp",EDGE,"E78.0"),sQuery(id+"F33.wireOp",EDGE,"E79.0"),sQuery(id+"F33.wireOp",EDGE,"E80.0"),sQuery(id+"F33.wireOp",EDGE,"E81.filletArc"),sQuery(id+"F33.wireOp",EDGE,"E82.filletArc"),sQuery(id+"F33.wireOp",EDGE,"E83.filletArc"),sQuery(id+"F33.wireOp",EDGE,"E84.filletArc")])],"isStart":false});
            var sketch = newSketch(context, id + "F35", { "sketchPlane" : qUnion([Q0])});
            skCircle(sketch, "E111.0", {"center": v(-350, -285) * mm, "radius": 10 * mm});
            skCircle(sketch, "E112.0", {"center": v(-350, 285) * mm, "radius": 10 * mm});
            skCircle(sketch, "E113.0", {"center": v(350, 285) * mm, "radius": 10 * mm});
            skCircle(sketch, "E114.0", {"center": v(350, -285) * mm, "radius": 10 * mm});
            skCircle(sketch, "E115", {"center": v(-350, -285) * mm, "radius": 104.3 * mm, "construction": true});
            skCircle(sketch, "E116", {"center": v(-350, -285) * mm, "radius": 79.86 * mm, "construction": true});
            skLineSegment(sketch, "E117.1.20.0", {"start": v(-429.64, -285.51) * mm, "end": v(-450.2, -285.65) * mm, "construction": true});
            skLineSegment(sketch, "E117.1.21.0", {"start": v(-434.23, -298.9) * mm, "end": v(-448.87, -301.32) * mm});
            skLineSegment(sketch, "E117.1.22.0", {"start": v(-431.51, -312.07) * mm, "end": v(-445.1, -316.59) * mm});
            skArc(sketch, "E118.trimOffspring", {"start": v(-434.23, -298.9) * mm, "mid": v(-433.13, -305.54) * mm, "end": v(-431.51, -312.07) * mm, "construction": true});
            skArc(sketch, "E119", {"start": v(-450.2, -285.65) * mm, "mid": v(-456.15, -294.05) * mm, "end": v(-448.87, -301.32) * mm});
            skPoint(sketch, "E119.third.point", {"position": v(-454.24, -288.17) * mm});
            skPoint(sketch, "E119.third.point.positionSnap0", {"position": v(-387.2, -288.17) * mm});
            skArc(sketch, "E120", {"start": v(-432.29, -312.33) * mm, "mid": v(-427.5, -303.83) * mm, "end": v(-436.08, -299.2) * mm});
            skPoint(sketch, "E120.third.point", {"position": v(-427.83, -302.91) * mm});
            skPoint(sketch, "E121.orphan", {"position": v(-456.33, -285.7) * mm});
            skPoint(sketch, "E122.orphan", {"position": v(-454.9, -302.32) * mm});
            skPoint(sketch, "E123.orphan", {"position": v(-428.58, -297.96) * mm});
            skPoint(sketch, "E124.orphan", {"position": v(-450.9, -318.52) * mm});
            skPoint(sketch, "E125.orphan", {"position": v(-425.59, -310.1) * mm});
            skArc(sketch, "E126.1.0", {"start": v(-445.1, -316.59) * mm, "mid": v(-448.16, -326.4) * mm, "end": v(-438.99, -331.08) * mm});
            skLineSegment(sketch, "E126.1.1", {"start": v(-425.82, -324.25) * mm, "end": v(-438.99, -331.08) * mm});
            skArc(sketch, "E126.1.2", {"start": v(-419.82, -336.42) * mm, "mid": v(-417.88, -326.85) * mm, "end": v(-427.48, -325.1) * mm});
            skLineSegment(sketch, "E126.1.3", {"start": v(-419.16, -335.93) * mm, "end": v(-430.69, -344.43) * mm});
            skArc(sketch, "E126.2.0", {"start": v(-430.69, -344.43) * mm, "mid": v(-430.55, -354.71) * mm, "end": v(-420.4, -356.32) * mm});
            skLineSegment(sketch, "E126.2.1", {"start": v(-409.98, -345.76) * mm, "end": v(-420.4, -356.32) * mm});
            skArc(sketch, "E126.2.2", {"start": v(-400.51, -355.47) * mm, "mid": v(-401.62, -345.78) * mm, "end": v(-411.3, -347.09) * mm});
            skLineSegment(sketch, "E126.2.3", {"start": v(-400.04, -354.81) * mm, "end": v(-408.37, -366.45) * mm});
            skArc(sketch, "E127.3.3.0", {"start": v(-408.37, -366.45) * mm, "mid": v(-405.07, -376.2) * mm, "end": v(-394.91, -374.58) * mm});
            skLineSegment(sketch, "E127.4.3.0", {"start": v(-388.27, -361.32) * mm, "end": v(-394.91, -374.58) * mm});
            skArc(sketch, "E127.7.3.0", {"start": v(-376.26, -367.63) * mm, "mid": v(-380.31, -358.76) * mm, "end": v(-389.1, -362.99) * mm});
            skLineSegment(sketch, "E127.11.3.0", {"start": v(-376.01, -366.86) * mm, "end": v(-380.34, -380.5) * mm});
            skArc(sketch, "E127.3.4.0", {"start": v(-380.34, -380.5) * mm, "mid": v(-374.2, -388.75) * mm, "end": v(-365.03, -384.08) * mm});
            skLineSegment(sketch, "E127.4.4.0", {"start": v(-362.81, -369.4) * mm, "end": v(-365.03, -384.08) * mm});
            skArc(sketch, "E127.7.4.0", {"start": v(-349.44, -371.7) * mm, "mid": v(-356.04, -364.52) * mm, "end": v(-363.1, -371.26) * mm});
            skLineSegment(sketch, "E127.11.4.0", {"start": v(-349.45, -370.89) * mm, "end": v(-349.35, -385.2) * mm});
            skArc(sketch, "E127.3.5.0", {"start": v(-349.35, -385.2) * mm, "mid": v(-340.95, -391.15) * mm, "end": v(-333.68, -383.87) * mm});
            skLineSegment(sketch, "E127.4.5.0", {"start": v(-336.1, -369.23) * mm, "end": v(-333.68, -383.87) * mm});
            skArc(sketch, "E127.7.5.0", {"start": v(-322.67, -367.29) * mm, "mid": v(-331.17, -362.5) * mm, "end": v(-335.8, -371.08) * mm});
            skLineSegment(sketch, "E127.11.5.0", {"start": v(-322.93, -366.51) * mm, "end": v(-318.41, -380.1) * mm});
            skArc(sketch, "E127.3.6.0", {"start": v(-318.41, -380.1) * mm, "mid": v(-308.6, -383.16) * mm, "end": v(-303.92, -373.99) * mm});
            skLineSegment(sketch, "E127.4.6.0", {"start": v(-310.75, -360.82) * mm, "end": v(-303.92, -373.99) * mm});
            skArc(sketch, "E127.7.6.0", {"start": v(-298.58, -354.82) * mm, "mid": v(-308.15, -352.88) * mm, "end": v(-309.9, -362.48) * mm});
            skLineSegment(sketch, "E127.11.6.0", {"start": v(-299.07, -354.16) * mm, "end": v(-290.57, -365.69) * mm});
            skArc(sketch, "E127.3.7.0", {"start": v(-290.57, -365.69) * mm, "mid": v(-280.29, -365.55) * mm, "end": v(-278.68, -355.4) * mm});
            skLineSegment(sketch, "E127.4.7.0", {"start": v(-289.24, -344.98) * mm, "end": v(-278.68, -355.4) * mm});
            skArc(sketch, "E127.7.7.0", {"start": v(-279.53, -335.51) * mm, "mid": v(-289.22, -336.62) * mm, "end": v(-287.91, -346.3) * mm});
            skLineSegment(sketch, "E127.11.7.0", {"start": v(-280.19, -335.04) * mm, "end": v(-268.55, -343.37) * mm});
            skArc(sketch, "E127.3.8.0", {"start": v(-268.55, -343.37) * mm, "mid": v(-258.8, -340.07) * mm, "end": v(-260.42, -329.91) * mm});
            skLineSegment(sketch, "E127.4.8.0", {"start": v(-273.68, -323.27) * mm, "end": v(-260.42, -329.91) * mm});
            skArc(sketch, "E127.7.8.0", {"start": v(-267.37, -311.26) * mm, "mid": v(-276.24, -315.31) * mm, "end": v(-272.01, -324.1) * mm});
            skLineSegment(sketch, "E127.11.8.0", {"start": v(-268.14, -311.01) * mm, "end": v(-254.5, -315.34) * mm});
            skArc(sketch, "E127.3.9.0", {"start": v(-254.5, -315.34) * mm, "mid": v(-246.25, -309.2) * mm, "end": v(-250.92, -300.03) * mm});
            skLineSegment(sketch, "E127.4.9.0", {"start": v(-265.6, -297.81) * mm, "end": v(-250.92, -300.03) * mm});
            skArc(sketch, "E127.7.9.0", {"start": v(-263.3, -284.44) * mm, "mid": v(-270.48, -291.04) * mm, "end": v(-263.74, -298.1) * mm});
            skLineSegment(sketch, "E127.11.9.0", {"start": v(-264.11, -284.45) * mm, "end": v(-249.8, -284.35) * mm});
            skArc(sketch, "E127.3.10.0", {"start": v(-249.8, -284.35) * mm, "mid": v(-243.85, -275.95) * mm, "end": v(-251.13, -268.68) * mm});
            skLineSegment(sketch, "E127.4.10.0", {"start": v(-265.77, -271.1) * mm, "end": v(-251.13, -268.68) * mm});
            skArc(sketch, "E127.7.10.0", {"start": v(-267.71, -257.67) * mm, "mid": v(-272.5, -266.17) * mm, "end": v(-263.92, -270.8) * mm});
            skLineSegment(sketch, "E127.11.10.0", {"start": v(-268.49, -257.93) * mm, "end": v(-254.9, -253.41) * mm});
            skArc(sketch, "E127.3.11.0", {"start": v(-254.9, -253.41) * mm, "mid": v(-251.84, -243.6) * mm, "end": v(-261.01, -238.92) * mm});
            skLineSegment(sketch, "E127.4.11.0", {"start": v(-274.18, -245.75) * mm, "end": v(-261.01, -238.92) * mm});
            skArc(sketch, "E127.7.11.0", {"start": v(-280.18, -233.58) * mm, "mid": v(-282.12, -243.15) * mm, "end": v(-272.52, -244.9) * mm});
            skLineSegment(sketch, "E127.11.11.0", {"start": v(-280.84, -234.07) * mm, "end": v(-269.31, -225.57) * mm});
            skArc(sketch, "E127.3.12.0", {"start": v(-269.31, -225.57) * mm, "mid": v(-269.45, -215.29) * mm, "end": v(-279.6, -213.68) * mm});
            skLineSegment(sketch, "E127.4.12.0", {"start": v(-290.02, -224.24) * mm, "end": v(-279.6, -213.68) * mm});
            skArc(sketch, "E127.7.12.0", {"start": v(-299.49, -214.53) * mm, "mid": v(-298.38, -224.22) * mm, "end": v(-288.7, -222.91) * mm});
            skLineSegment(sketch, "E127.11.12.0", {"start": v(-299.96, -215.19) * mm, "end": v(-291.63, -203.55) * mm});
            skArc(sketch, "E127.3.13.0", {"start": v(-291.63, -203.55) * mm, "mid": v(-294.93, -193.8) * mm, "end": v(-305.09, -195.42) * mm});
            skLineSegment(sketch, "E127.4.13.0", {"start": v(-311.73, -208.68) * mm, "end": v(-305.09, -195.42) * mm});
            skArc(sketch, "E127.7.13.0", {"start": v(-323.74, -202.37) * mm, "mid": v(-319.69, -211.24) * mm, "end": v(-310.9, -207.01) * mm});
            skLineSegment(sketch, "E127.11.13.0", {"start": v(-323.99, -203.14) * mm, "end": v(-319.66, -189.5) * mm});
            skArc(sketch, "E127.3.14.0", {"start": v(-319.66, -189.5) * mm, "mid": v(-325.8, -181.25) * mm, "end": v(-334.97, -185.92) * mm});
            skLineSegment(sketch, "E127.4.14.0", {"start": v(-337.19, -200.6) * mm, "end": v(-334.97, -185.92) * mm});
            skArc(sketch, "E127.7.14.0", {"start": v(-350.56, -198.3) * mm, "mid": v(-343.96, -205.48) * mm, "end": v(-336.9, -198.74) * mm});
            skLineSegment(sketch, "E127.11.14.0", {"start": v(-350.55, -199.11) * mm, "end": v(-350.65, -184.8) * mm});
            skArc(sketch, "E127.3.15.0", {"start": v(-350.65, -184.8) * mm, "mid": v(-359.05, -178.85) * mm, "end": v(-366.32, -186.13) * mm});
            skLineSegment(sketch, "E127.4.15.0", {"start": v(-363.9, -200.77) * mm, "end": v(-366.32, -186.13) * mm});
            skArc(sketch, "E127.7.15.0", {"start": v(-377.33, -202.71) * mm, "mid": v(-368.83, -207.5) * mm, "end": v(-364.2, -198.92) * mm});
            skLineSegment(sketch, "E127.11.15.0", {"start": v(-377.07, -203.49) * mm, "end": v(-381.59, -189.9) * mm});
            skArc(sketch, "E127.3.16.0", {"start": v(-381.59, -189.9) * mm, "mid": v(-391.4, -186.84) * mm, "end": v(-396.08, -196.01) * mm});
            skLineSegment(sketch, "E127.4.16.0", {"start": v(-389.25, -209.18) * mm, "end": v(-396.08, -196.01) * mm});
            skArc(sketch, "E127.7.16.0", {"start": v(-401.42, -215.18) * mm, "mid": v(-391.85, -217.12) * mm, "end": v(-390.1, -207.52) * mm});
            skLineSegment(sketch, "E127.11.16.0", {"start": v(-400.93, -215.84) * mm, "end": v(-409.43, -204.31) * mm});
            skArc(sketch, "E127.3.17.0", {"start": v(-409.43, -204.31) * mm, "mid": v(-419.71, -204.45) * mm, "end": v(-421.32, -214.6) * mm});
            skLineSegment(sketch, "E127.4.17.0", {"start": v(-410.76, -225.02) * mm, "end": v(-421.32, -214.6) * mm});
            skArc(sketch, "E127.7.17.0", {"start": v(-420.47, -234.49) * mm, "mid": v(-410.78, -233.38) * mm, "end": v(-412.09, -223.7) * mm});
            skLineSegment(sketch, "E127.11.17.0", {"start": v(-419.81, -234.96) * mm, "end": v(-431.45, -226.63) * mm});
            skArc(sketch, "E127.3.18.0", {"start": v(-431.45, -226.63) * mm, "mid": v(-441.2, -229.93) * mm, "end": v(-439.58, -240.09) * mm});
            skLineSegment(sketch, "E127.4.18.0", {"start": v(-426.32, -246.73) * mm, "end": v(-439.58, -240.09) * mm});
            skArc(sketch, "E127.7.18.0", {"start": v(-432.63, -258.74) * mm, "mid": v(-423.76, -254.69) * mm, "end": v(-427.99, -245.9) * mm});
            skLineSegment(sketch, "E127.11.18.0", {"start": v(-431.86, -258.99) * mm, "end": v(-445.5, -254.66) * mm});
            skArc(sketch, "E127.3.19.0", {"start": v(-445.5, -254.66) * mm, "mid": v(-453.75, -260.8) * mm, "end": v(-449.08, -269.97) * mm});
            skLineSegment(sketch, "E127.4.19.0", {"start": v(-434.4, -272.19) * mm, "end": v(-449.08, -269.97) * mm});
            skArc(sketch, "E127.7.19.0", {"start": v(-436.7, -285.56) * mm, "mid": v(-429.52, -278.96) * mm, "end": v(-436.26, -271.9) * mm});
            skLineSegment(sketch, "E127.11.19.0", {"start": v(-435.89, -285.55) * mm, "end": v(-450.2, -285.65) * mm});
            skPoint(sketch, "E128.orphan", {"position": v(-393.16, -371.08) * mm});
            skPoint(sketch, "E129.orphan", {"position": v(-379.16, -376.78) * mm});
            skPoint(sketch, "E130.orphan", {"position": v(-364.44, -380.2) * mm});
            skPoint(sketch, "E131.orphan", {"position": v(-349.37, -381.3) * mm});
            skPoint(sketch, "E132.orphan", {"position": v(-334.32, -380) * mm});
            skPoint(sketch, "E133.orphan", {"position": v(-319.65, -376.4) * mm});
            skPoint(sketch, "E134.orphan", {"position": v(-305.73, -370.5) * mm});
            skPoint(sketch, "E135.orphan", {"position": v(-292.89, -362.54) * mm});
            skPoint(sketch, "E136.orphan", {"position": v(-281.47, -352.64) * mm});
            skPoint(sketch, "E137.orphan", {"position": v(-271.72, -341.1) * mm});
            skPoint(sketch, "E138.orphan", {"position": v(-263.92, -328.16) * mm});
            skPoint(sketch, "E139.orphan", {"position": v(-258.22, -314.16) * mm});
            skPoint(sketch, "E140.orphan", {"position": v(-254.8, -299.44) * mm});
            skPoint(sketch, "E141.orphan", {"position": v(-253.7, -284.37) * mm});
            skPoint(sketch, "E142.orphan", {"position": v(-255, -269.32) * mm});
            skPoint(sketch, "E143.orphan", {"position": v(-258.6, -254.65) * mm});
            skPoint(sketch, "E144.orphan", {"position": v(-264.5, -240.73) * mm});
            skPoint(sketch, "E145.orphan", {"position": v(-272.46, -227.89) * mm});
            skPoint(sketch, "E146.orphan", {"position": v(-282.36, -216.47) * mm});
            skPoint(sketch, "E147.orphan", {"position": v(-293.9, -206.72) * mm});
            skPoint(sketch, "E148.orphan", {"position": v(-306.84, -198.92) * mm});
            skPoint(sketch, "E149.orphan", {"position": v(-320.84, -193.22) * mm});
            skPoint(sketch, "E150.orphan", {"position": v(-335.56, -189.8) * mm});
            skPoint(sketch, "E151.orphan", {"position": v(-350.63, -188.7) * mm});
            skPoint(sketch, "E152.orphan", {"position": v(-365.68, -190) * mm});
            skPoint(sketch, "E153.orphan", {"position": v(-380.35, -193.6) * mm});
            skPoint(sketch, "E154.orphan", {"position": v(-394.27, -199.5) * mm});
            skPoint(sketch, "E155.orphan", {"position": v(-407.11, -207.46) * mm});
            skPoint(sketch, "E156.orphan", {"position": v(-418.53, -217.36) * mm});
            skPoint(sketch, "E157.orphan", {"position": v(-428.28, -228.9) * mm});
            skPoint(sketch, "E158.orphan", {"position": v(-436.08, -241.84) * mm});
            skPoint(sketch, "E159.orphan", {"position": v(-441.78, -255.84) * mm});
            skPoint(sketch, "E160.orphan", {"position": v(-445.2, -270.56) * mm});
            skPoint(sketch, "E161.orphan", {"position": v(-446.3, -285.63) * mm});
            skPoint(sketch, "E162.orphan", {"position": v(-445, -300.68) * mm});
            skPoint(sketch, "E163.orphan", {"position": v(-441.4, -315.35) * mm});
            skPoint(sketch, "E164.orphan", {"position": v(-435.5, -329.27) * mm});
            skPoint(sketch, "E165.orphan", {"position": v(-427.54, -342.11) * mm});
            skPoint(sketch, "E166.orphan", {"position": v(-417.64, -353.53) * mm});
            skPoint(sketch, "E167.orphan", {"position": v(-406.1, -363.28) * mm});
            skLineSegment(sketch, "E168", {"start": v(-350, -285) * mm, "end": v(0, 0) * mm, "construction": true});
            skLineSegment(sketch, "E169", {"start": v(-293.8, -213.8) * mm, "end": v(0, 0) * mm, "construction": true});
            skLineSegment(sketch, "E170", {"start": v(-293.9, -206.72) * mm, "end": v(-282.36, -216.47) * mm, "construction": true});
            skLineSegment(sketch, "E171", {"start": v(-288.93, -200.46) * mm, "end": v(-279.6, -213.27) * mm, "construction": true});
            skLineSegment(sketch, "E172", {"start": v(-279.6, -213.27) * mm, "end": v(-276.56, -210.95) * mm, "construction": true});
            skPoint(sketch, "E173.center.orphan", {"position": v(-290.7, -192.13) * mm});
            skPoint(sketch, "E174.orphan", {"position": v(0, 0) * mm});
            skCircle(sketch, "E175", {"center": v(0, 0) * mm, "radius": 362.68 * mm});
            skCircle(sketch, "E176", {"center": v(0, 0) * mm, "radius": 314.95 * mm});
            skSolve(sketch);
        }
        {
            var Q0;
            {var subQ40=sQuery(id+"F35.wireOp",EDGE,"E127.3.10.0");Q0=makeQuery(id+"F35.imprint","IMPRINT",FACE,{"disambiguationData":[TD([[makeQuery(id+"F35.imprint","IMPRINT",EDGE,{"derivedFrom":subQ40}),1.0]])]});}
            var Q1;
            {var subQ70=sQuery(id+"F35.wireOp",EDGE,"E119");Q1=makeQuery(id+"F35.imprint","IMPRINT",FACE,{"disambiguationData":[TD([[makeQuery(id+"F35.imprint","IMPRINT",EDGE,{"derivedFrom":subQ70}),1.0]])]});}
            var Q2;
            {var subQ0=sQuery(id+"F35.wireOp",EDGE,"E127.3.13.0");Q2=makeQuery(id+"F35.imprint","IMPRINT",FACE,{"disambiguationData":[TD([[makeQuery(id+"F35.imprint","IMPRINT",EDGE,{"derivedFrom":subQ0}),1.0]])]});}
            var Q3;
            {var subQ0=sQuery(id+"F35.wireOp",EDGE,"E127.3.12.0");Q3=makeQuery(id+"F35.imprint","IMPRINT",FACE,{"disambiguationData":[TD([[makeQuery(id+"F35.imprint","IMPRINT",EDGE,{"derivedFrom":subQ0}),1.0]])]});}
            var Q4;
            {var subQ0=sQuery(id+"F35.wireOp",EDGE,"E127.3.11.0");Q4=makeQuery(id+"F35.imprint","IMPRINT",FACE,{"disambiguationData":[TD([[makeQuery(id+"F35.imprint","IMPRINT",EDGE,{"derivedFrom":subQ0}),1.0]])]});}
            var Q5;
            {var subQ3=sQuery(id+"F35.wireOp",EDGE,"E127.3.15.0");Q5=makeQuery(id+"F35.imprint","IMPRINT",FACE,{"disambiguationData":[TD([[makeQuery(id+"F35.imprint","IMPRINT",EDGE,{"derivedFrom":subQ3}),1.0]])]});}
            var Q6;
            {var subQ1=sQuery(id+"F35.wireOp",EDGE,"E127.3.14.0");Q6=makeQuery(id+"F35.imprint","IMPRINT",FACE,{"disambiguationData":[TD([[makeQuery(id+"F35.imprint","IMPRINT",EDGE,{"derivedFrom":subQ1}),1.0]])]});}
            extrude(context, id + "F36", {"entities" : qUnion([Q0, Q1, Q2, Q3, Q4, Q5, Q6]), "depth" : 15 * mm, "offsetDistance" : 25 * mm});
        }
        {
            var Q0;
            Q0=makeQuery(id+"F36.opExtrude","SWEPT_BODY",BODY,{"disambiguationData":[OSD([sQuery(id+"F35.wireOp",EDGE,"E111.0"),sQuery(id+"F35.wireOp",EDGE,"E117.1.21.0"),sQuery(id+"F35.wireOp",EDGE,"E117.1.22.0"),sQuery(id+"F35.wireOp",EDGE,"E119"),sQuery(id+"F35.wireOp",EDGE,"E120"),sQuery(id+"F35.wireOp",EDGE,"E126.1.0"),sQuery(id+"F35.wireOp",EDGE,"E126.1.1"),sQuery(id+"F35.wireOp",EDGE,"E126.1.2"),sQuery(id+"F35.wireOp",EDGE,"E126.1.3"),sQuery(id+"F35.wireOp",EDGE,"E126.2.0"),sQuery(id+"F35.wireOp",EDGE,"E126.2.1"),sQuery(id+"F35.wireOp",EDGE,"E126.2.2"),sQuery(id+"F35.wireOp",EDGE,"E126.2.3"),sQuery(id+"F35.wireOp",EDGE,"E127.3.3.0"),sQuery(id+"F35.wireOp",EDGE,"E127.4.3.0"),sQuery(id+"F35.wireOp",EDGE,"E127.7.3.0"),sQuery(id+"F35.wireOp",EDGE,"E127.11.3.0"),sQuery(id+"F35.wireOp",EDGE,"E127.3.4.0"),sQuery(id+"F35.wireOp",EDGE,"E127.4.4.0"),sQuery(id+"F35.wireOp",EDGE,"E127.7.4.0"),sQuery(id+"F35.wireOp",EDGE,"E127.11.4.0"),sQuery(id+"F35.wireOp",EDGE,"E127.3.5.0"),sQuery(id+"F35.wireOp",EDGE,"E127.4.5.0"),sQuery(id+"F35.wireOp",EDGE,"E127.7.5.0"),sQuery(id+"F35.wireOp",EDGE,"E127.11.5.0"),sQuery(id+"F35.wireOp",EDGE,"E127.3.6.0"),sQuery(id+"F35.wireOp",EDGE,"E127.4.6.0"),sQuery(id+"F35.wireOp",EDGE,"E127.7.6.0"),sQuery(id+"F35.wireOp",EDGE,"E127.11.6.0"),sQuery(id+"F35.wireOp",EDGE,"E127.3.7.0"),sQuery(id+"F35.wireOp",EDGE,"E127.4.7.0"),sQuery(id+"F35.wireOp",EDGE,"E127.7.7.0"),sQuery(id+"F35.wireOp",EDGE,"E127.11.7.0"),sQuery(id+"F35.wireOp",EDGE,"E127.3.8.0"),sQuery(id+"F35.wireOp",EDGE,"E127.4.8.0"),sQuery(id+"F35.wireOp",EDGE,"E127.7.8.0"),sQuery(id+"F35.wireOp",EDGE,"E127.11.8.0"),sQuery(id+"F35.wireOp",EDGE,"E127.3.9.0"),sQuery(id+"F35.wireOp",EDGE,"E127.4.9.0"),sQuery(id+"F35.wireOp",EDGE,"E127.7.9.0"),sQuery(id+"F35.wireOp",EDGE,"E127.11.9.0"),sQuery(id+"F35.wireOp",EDGE,"E127.3.10.0"),sQuery(id+"F35.wireOp",EDGE,"E127.4.10.0"),sQuery(id+"F35.wireOp",EDGE,"E127.7.10.0"),sQuery(id+"F35.wireOp",EDGE,"E127.11.10.0"),sQuery(id+"F35.wireOp",EDGE,"E127.3.11.0"),sQuery(id+"F35.wireOp",EDGE,"E127.4.11.0"),sQuery(id+"F35.wireOp",EDGE,"E127.7.11.0"),sQuery(id+"F35.wireOp",EDGE,"E127.11.11.0"),sQuery(id+"F35.wireOp",EDGE,"E127.3.12.0"),sQuery(id+"F35.wireOp",EDGE,"E127.4.12.0"),sQuery(id+"F35.wireOp",EDGE,"E127.7.12.0"),sQuery(id+"F35.wireOp",EDGE,"E127.11.12.0"),sQuery(id+"F35.wireOp",EDGE,"E127.3.13.0"),sQuery(id+"F35.wireOp",EDGE,"E127.4.13.0"),sQuery(id+"F35.wireOp",EDGE,"E127.7.13.0"),sQuery(id+"F35.wireOp",EDGE,"E127.11.13.0"),sQuery(id+"F35.wireOp",EDGE,"E127.3.14.0"),sQuery(id+"F35.wireOp",EDGE,"E127.4.14.0"),sQuery(id+"F35.wireOp",EDGE,"E127.7.14.0"),sQuery(id+"F35.wireOp",EDGE,"E127.11.14.0"),sQuery(id+"F35.wireOp",EDGE,"E127.3.15.0"),sQuery(id+"F35.wireOp",EDGE,"E127.4.15.0"),sQuery(id+"F35.wireOp",EDGE,"E127.7.15.0"),sQuery(id+"F35.wireOp",EDGE,"E127.11.15.0"),sQuery(id+"F35.wireOp",EDGE,"E127.3.16.0"),sQuery(id+"F35.wireOp",EDGE,"E127.4.16.0"),sQuery(id+"F35.wireOp",EDGE,"E127.7.16.0"),sQuery(id+"F35.wireOp",EDGE,"E127.11.16.0"),sQuery(id+"F35.wireOp",EDGE,"E127.3.17.0"),sQuery(id+"F35.wireOp",EDGE,"E127.4.17.0"),sQuery(id+"F35.wireOp",EDGE,"E127.7.17.0"),sQuery(id+"F35.wireOp",EDGE,"E127.11.17.0"),sQuery(id+"F35.wireOp",EDGE,"E127.3.18.0"),sQuery(id+"F35.wireOp",EDGE,"E127.4.18.0"),sQuery(id+"F35.wireOp",EDGE,"E127.7.18.0"),sQuery(id+"F35.wireOp",EDGE,"E127.11.18.0"),sQuery(id+"F35.wireOp",EDGE,"E127.3.19.0"),sQuery(id+"F35.wireOp",EDGE,"E127.4.19.0"),sQuery(id+"F35.wireOp",EDGE,"E127.7.19.0"),sQuery(id+"F35.wireOp",EDGE,"E127.11.19.0")])]});
            var Q1;
            Q1=makeQuery(id+"FxZatVkshsRlc5E_12.opPattern","COPY",BODY,{"derivedFrom":makeQuery(id+"F36.opExtrude","SWEPT_BODY",BODY,{"disambiguationData":[OSD([sQuery(id+"F35.wireOp",EDGE,"E111.0"),sQuery(id+"F35.wireOp",EDGE,"E117.1.21.0"),sQuery(id+"F35.wireOp",EDGE,"E117.1.22.0"),sQuery(id+"F35.wireOp",EDGE,"E119"),sQuery(id+"F35.wireOp",EDGE,"E120"),sQuery(id+"F35.wireOp",EDGE,"E126.1.0"),sQuery(id+"F35.wireOp",EDGE,"E126.1.1"),sQuery(id+"F35.wireOp",EDGE,"E126.1.2"),sQuery(id+"F35.wireOp",EDGE,"E126.1.3"),sQuery(id+"F35.wireOp",EDGE,"E126.2.0"),sQuery(id+"F35.wireOp",EDGE,"E126.2.1"),sQuery(id+"F35.wireOp",EDGE,"E126.2.2"),sQuery(id+"F35.wireOp",EDGE,"E126.2.3"),sQuery(id+"F35.wireOp",EDGE,"E127.3.3.0"),sQuery(id+"F35.wireOp",EDGE,"E127.4.3.0"),sQuery(id+"F35.wireOp",EDGE,"E127.7.3.0"),sQuery(id+"F35.wireOp",EDGE,"E127.11.3.0"),sQuery(id+"F35.wireOp",EDGE,"E127.3.4.0"),sQuery(id+"F35.wireOp",EDGE,"E127.4.4.0"),sQuery(id+"F35.wireOp",EDGE,"E127.7.4.0"),sQuery(id+"F35.wireOp",EDGE,"E127.11.4.0"),sQuery(id+"F35.wireOp",EDGE,"E127.3.5.0"),sQuery(id+"F35.wireOp",EDGE,"E127.4.5.0"),sQuery(id+"F35.wireOp",EDGE,"E127.7.5.0"),sQuery(id+"F35.wireOp",EDGE,"E127.11.5.0"),sQuery(id+"F35.wireOp",EDGE,"E127.3.6.0"),sQuery(id+"F35.wireOp",EDGE,"E127.4.6.0"),sQuery(id+"F35.wireOp",EDGE,"E127.7.6.0"),sQuery(id+"F35.wireOp",EDGE,"E127.11.6.0"),sQuery(id+"F35.wireOp",EDGE,"E127.3.7.0"),sQuery(id+"F35.wireOp",EDGE,"E127.4.7.0"),sQuery(id+"F35.wireOp",EDGE,"E127.7.7.0"),sQuery(id+"F35.wireOp",EDGE,"E127.11.7.0"),sQuery(id+"F35.wireOp",EDGE,"E127.3.8.0"),sQuery(id+"F35.wireOp",EDGE,"E127.4.8.0"),sQuery(id+"F35.wireOp",EDGE,"E127.7.8.0"),sQuery(id+"F35.wireOp",EDGE,"E127.11.8.0"),sQuery(id+"F35.wireOp",EDGE,"E127.3.9.0"),sQuery(id+"F35.wireOp",EDGE,"E127.4.9.0"),sQuery(id+"F35.wireOp",EDGE,"E127.7.9.0"),sQuery(id+"F35.wireOp",EDGE,"E127.11.9.0"),sQuery(id+"F35.wireOp",EDGE,"E127.3.10.0"),sQuery(id+"F35.wireOp",EDGE,"E127.4.10.0"),sQuery(id+"F35.wireOp",EDGE,"E127.7.10.0"),sQuery(id+"F35.wireOp",EDGE,"E127.11.10.0"),sQuery(id+"F35.wireOp",EDGE,"E127.3.11.0"),sQuery(id+"F35.wireOp",EDGE,"E127.4.11.0"),sQuery(id+"F35.wireOp",EDGE,"E127.7.11.0"),sQuery(id+"F35.wireOp",EDGE,"E127.11.11.0"),sQuery(id+"F35.wireOp",EDGE,"E127.3.12.0"),sQuery(id+"F35.wireOp",EDGE,"E127.4.12.0"),sQuery(id+"F35.wireOp",EDGE,"E127.7.12.0"),sQuery(id+"F35.wireOp",EDGE,"E127.11.12.0"),sQuery(id+"F35.wireOp",EDGE,"E127.3.13.0"),sQuery(id+"F35.wireOp",EDGE,"E127.4.13.0"),sQuery(id+"F35.wireOp",EDGE,"E127.7.13.0"),sQuery(id+"F35.wireOp",EDGE,"E127.11.13.0"),sQuery(id+"F35.wireOp",EDGE,"E127.3.14.0"),sQuery(id+"F35.wireOp",EDGE,"E127.4.14.0"),sQuery(id+"F35.wireOp",EDGE,"E127.7.14.0"),sQuery(id+"F35.wireOp",EDGE,"E127.11.14.0"),sQuery(id+"F35.wireOp",EDGE,"E127.3.15.0"),sQuery(id+"F35.wireOp",EDGE,"E127.4.15.0"),sQuery(id+"F35.wireOp",EDGE,"E127.7.15.0"),sQuery(id+"F35.wireOp",EDGE,"E127.11.15.0"),sQuery(id+"F35.wireOp",EDGE,"E127.3.16.0"),sQuery(id+"F35.wireOp",EDGE,"E127.4.16.0"),sQuery(id+"F35.wireOp",EDGE,"E127.7.16.0"),sQuery(id+"F35.wireOp",EDGE,"E127.11.16.0"),sQuery(id+"F35.wireOp",EDGE,"E127.3.17.0"),sQuery(id+"F35.wireOp",EDGE,"E127.4.17.0"),sQuery(id+"F35.wireOp",EDGE,"E127.7.17.0"),sQuery(id+"F35.wireOp",EDGE,"E127.11.17.0"),sQuery(id+"F35.wireOp",EDGE,"E127.3.18.0"),sQuery(id+"F35.wireOp",EDGE,"E127.4.18.0"),sQuery(id+"F35.wireOp",EDGE,"E127.7.18.0"),sQuery(id+"F35.wireOp",EDGE,"E127.11.18.0"),sQuery(id+"F35.wireOp",EDGE,"E127.3.19.0"),sQuery(id+"F35.wireOp",EDGE,"E127.4.19.0"),sQuery(id+"F35.wireOp",EDGE,"E127.7.19.0"),sQuery(id+"F35.wireOp",EDGE,"E127.11.19.0")])]}),"instanceName":"1"});
            var Q2;
            Q2=qCreatedBy(makeId("Right.planeOp"),FACE);
            mirror(context, id + "F37", {"entities" : qUnion([Q0, Q1]), "mirrorPlane" : qUnion([Q2])});
        }
        {
            var Q0;
            {var subQ4=sQuery(id+"F35.wireOp",EDGE,"E127.3.11.0");Q0=makeQuery(id+"F35.imprint","IMPRINT",FACE,{"disambiguationData":[TD([[makeQuery(id+"F35.imprint","IMPRINT",EDGE,{"derivedFrom":subQ4}),-1.0]])]});}
            var Q1;
            {var subQ0=sQuery(id+"F35.wireOp",EDGE,"E175");var subQ1=makeQuery(id+"F34.opExtrude","CAP_EDGE",EDGE,{"disambiguationData":[OSD([sQuery(id+"F33.wireOp",EDGE,"E76.2")])],"isStart":false});var subQ2=makeQuery(id+"F35.imprint","INTERSECT",VERTEX,{"disambiguationData":[OD(0.0)],"derivedFrom":[subQ1,subQ0]});Q1=makeQuery(id+"F35.imprint","IMPRINT",FACE,{"disambiguationData":[TD([[makeQuery(id+"F35.imprint","IMPRINT",EDGE,{"disambiguationData":[TD([[subQ2,-1.0]])],"derivedFrom":subQ0}),1.0]])]});}
            var Q2;
            {var subQ0=sQuery(id+"F35.wireOp",EDGE,"E175");var subQ1=makeQuery(id+"F34.opExtrude","CAP_EDGE",EDGE,{"disambiguationData":[OSD([sQuery(id+"F33.wireOp",EDGE,"E76.0")])],"isStart":false});var subQ2=makeQuery(id+"F35.imprint","INTERSECT",VERTEX,{"disambiguationData":[OD(0.0)],"derivedFrom":[subQ1,subQ0]});Q2=makeQuery(id+"F35.imprint","IMPRINT",FACE,{"disambiguationData":[TD([[makeQuery(id+"F35.imprint","IMPRINT",EDGE,{"disambiguationData":[TD([[subQ2,1.0]])],"derivedFrom":subQ0}),1.0]])]});}
            var Q3;
            {var subQ0=sQuery(id+"F35.wireOp",EDGE,"E175");var subQ1=makeQuery(id+"F34.opExtrude","CAP_EDGE",EDGE,{"disambiguationData":[OSD([sQuery(id+"F33.wireOp",EDGE,"E76.2")])],"isStart":false});var subQ2=makeQuery(id+"F35.imprint","INTERSECT",VERTEX,{"disambiguationData":[OD(0.0)],"derivedFrom":[subQ1,subQ0]});Q3=makeQuery(id+"F35.imprint","IMPRINT",FACE,{"disambiguationData":[TD([[makeQuery(id+"F35.imprint","IMPRINT",EDGE,{"disambiguationData":[TD([[subQ2,1.0]])],"derivedFrom":subQ0}),1.0]])]});}
            var Q4;
            {var subQ0=sQuery(id+"F35.wireOp",EDGE,"E175");var subQ1=makeQuery(id+"F34.opExtrude","CAP_EDGE",EDGE,{"disambiguationData":[OSD([sQuery(id+"F33.wireOp",EDGE,"E96.trimOffspring")])],"isStart":false});var subQ2=makeQuery(id+"F35.imprint","INTERSECT",VERTEX,{"disambiguationData":[OD(1.0)],"derivedFrom":[subQ1,subQ0]});Q4=makeQuery(id+"F35.imprint","IMPRINT",FACE,{"disambiguationData":[TD([[makeQuery(id+"F35.imprint","IMPRINT",EDGE,{"disambiguationData":[TD([[subQ2,-1.0]])],"derivedFrom":subQ0}),1.0]])]});}
            var Q5;
            {var subQ0=sQuery(id+"F35.wireOp",EDGE,"E175");var subQ1=makeQuery(id+"F34.opExtrude","CAP_EDGE",EDGE,{"disambiguationData":[OSD([sQuery(id+"F33.wireOp",EDGE,"E94.trimOffspring")])],"isStart":false});var subQ2=makeQuery(id+"F35.imprint","INTERSECT",VERTEX,{"derivedFrom":[subQ1,subQ0]});Q5=makeQuery(id+"F35.imprint","IMPRINT",FACE,{"disambiguationData":[TD([[makeQuery(id+"F35.imprint","IMPRINT",EDGE,{"disambiguationData":[TD([[subQ2,-1.0]])],"derivedFrom":subQ0}),1.0]])]});}
            var Q6;
            {var subQ1=makeQuery(id+"F34.opExtrude","CAP_EDGE",EDGE,{"disambiguationData":[OSD([sQuery(id+"F33.wireOp",EDGE,"E93.trimOffspring")])],"isStart":false});var subQ5=sQuery(id+"F35.wireOp",EDGE,"E175");var subQ10=makeQuery(id+"F35.imprint","INTERSECT",VERTEX,{"derivedFrom":[subQ1,subQ5]});Q6=makeQuery(id+"F35.imprint","IMPRINT",FACE,{"disambiguationData":[TD([[makeQuery(id+"F35.imprint","IMPRINT",EDGE,{"disambiguationData":[TD([[subQ10,1.0]])],"derivedFrom":subQ5}),1.0]])]});}
            var Q7;
            {var subQ0=sQuery(id+"F35.wireOp",EDGE,"E175");var subQ1=makeQuery(id+"F34.opExtrude","CAP_EDGE",EDGE,{"disambiguationData":[OSD([sQuery(id+"F33.wireOp",EDGE,"E95.2")])],"isStart":false});var subQ2=makeQuery(id+"F35.imprint","INTERSECT",VERTEX,{"disambiguationData":[OD(0.0)],"derivedFrom":[subQ1,subQ0]});Q7=makeQuery(id+"F35.imprint","IMPRINT",FACE,{"disambiguationData":[TD([[makeQuery(id+"F35.imprint","IMPRINT",EDGE,{"disambiguationData":[TD([[subQ2,1.0]])],"derivedFrom":subQ0}),1.0]])]});}
            var Q8;
            {var subQ0=sQuery(id+"F35.wireOp",EDGE,"E175");var subQ1=makeQuery(id+"F34.opExtrude","CAP_EDGE",EDGE,{"disambiguationData":[OSD([sQuery(id+"F33.wireOp",EDGE,"E93.trimOffspring")])],"isStart":false});var subQ2=makeQuery(id+"F35.imprint","INTERSECT",VERTEX,{"derivedFrom":[subQ1,subQ0]});Q8=makeQuery(id+"F35.imprint","IMPRINT",FACE,{"disambiguationData":[TD([[makeQuery(id+"F35.imprint","IMPRINT",EDGE,{"disambiguationData":[TD([[subQ2,-1.0]])],"derivedFrom":subQ0}),1.0]])]});}
            var Q9;
            {var subQ0=sQuery(id+"F35.wireOp",EDGE,"E175");var subQ1=makeQuery(id+"F34.opExtrude","CAP_EDGE",EDGE,{"disambiguationData":[OSD([sQuery(id+"F33.wireOp",EDGE,"E90.trimOffspring")])],"isStart":false});var subQ2=makeQuery(id+"F35.imprint","INTERSECT",VERTEX,{"derivedFrom":[subQ1,subQ0]});Q9=makeQuery(id+"F35.imprint","IMPRINT",FACE,{"disambiguationData":[TD([[makeQuery(id+"F35.imprint","IMPRINT",EDGE,{"disambiguationData":[TD([[subQ2,-1.0]])],"derivedFrom":subQ0}),1.0]])]});}
            var Q10;
            {var subQ0=sQuery(id+"F35.wireOp",EDGE,"E175");var subQ1=makeQuery(id+"F34.opExtrude","CAP_EDGE",EDGE,{"disambiguationData":[OSD([sQuery(id+"F33.wireOp",EDGE,"E76.0")])],"isStart":false});var subQ2=makeQuery(id+"F35.imprint","INTERSECT",VERTEX,{"disambiguationData":[OD(0.0)],"derivedFrom":[subQ1,subQ0]});Q10=makeQuery(id+"F35.imprint","IMPRINT",FACE,{"disambiguationData":[TD([[makeQuery(id+"F35.imprint","IMPRINT",EDGE,{"disambiguationData":[TD([[subQ2,-1.0]])],"derivedFrom":subQ0}),1.0]])]});}
            var Q11;
            {var subQ0=sQuery(id+"F35.wireOp",EDGE,"E175");var subQ1=makeQuery(id+"F34.opExtrude","CAP_EDGE",EDGE,{"disambiguationData":[OSD([sQuery(id+"F33.wireOp",EDGE,"E98.trimOffspring")])],"isStart":false});var subQ2=makeQuery(id+"F35.imprint","INTERSECT",VERTEX,{"disambiguationData":[OD(1.0)],"derivedFrom":[subQ1,subQ0]});Q11=makeQuery(id+"F35.imprint","IMPRINT",FACE,{"disambiguationData":[TD([[makeQuery(id+"F35.imprint","IMPRINT",EDGE,{"disambiguationData":[TD([[subQ2,-1.0]])],"derivedFrom":subQ0}),1.0]])]});}
            var Q12;
            {var subQ0=sQuery(id+"F35.wireOp",EDGE,"E175");var subQ1=makeQuery(id+"F34.opExtrude","CAP_EDGE",EDGE,{"disambiguationData":[OSD([sQuery(id+"F33.wireOp",EDGE,"E92.trimOffspring")])],"isStart":false});var subQ2=makeQuery(id+"F35.imprint","INTERSECT",VERTEX,{"derivedFrom":[subQ1,subQ0]});Q12=makeQuery(id+"F35.imprint","IMPRINT",FACE,{"disambiguationData":[TD([[makeQuery(id+"F35.imprint","IMPRINT",EDGE,{"disambiguationData":[TD([[subQ2,-1.0]])],"derivedFrom":subQ0}),1.0]])]});}
            var Q13;
            {var subQ8=sQuery(id+"F35.wireOp",EDGE,"E127.3.13.0");Q13=makeQuery(id+"F35.imprint","IMPRINT",FACE,{"disambiguationData":[TD([[makeQuery(id+"F35.imprint","IMPRINT",EDGE,{"derivedFrom":subQ8}),-1.0]])]});}
            var Q14;
            {var subQ0=sQuery(id+"F35.wireOp",EDGE,"E127.3.12.0");Q14=makeQuery(id+"F35.imprint","IMPRINT",FACE,{"disambiguationData":[TD([[makeQuery(id+"F35.imprint","IMPRINT",EDGE,{"derivedFrom":subQ0}),-1.0]])]});}
            var Q15;
            {var subQ0=sQuery(id+"F35.wireOp",EDGE,"E175");var subQ1=makeQuery(id+"F34.opExtrude","CAP_EDGE",EDGE,{"disambiguationData":[OSD([sQuery(id+"F33.wireOp",EDGE,"E97.trimOffspring")])],"isStart":false});var subQ2=makeQuery(id+"F35.imprint","INTERSECT",VERTEX,{"disambiguationData":[OD(0.0)],"derivedFrom":[subQ1,subQ0]});Q15=makeQuery(id+"F35.imprint","IMPRINT",FACE,{"disambiguationData":[TD([[makeQuery(id+"F35.imprint","IMPRINT",EDGE,{"disambiguationData":[TD([[subQ2,-1.0]])],"derivedFrom":subQ0}),1.0]])]});}
            extrude(context, id + "F38", {"entities" : qUnion([Q0, Q1, Q2, Q3, Q4, Q5, Q6, Q7, Q8, Q9, Q10, Q11, Q12, Q13, Q14, Q15]), "depth" : 15 * mm, "offsetDistance" : 25 * mm});
        }
        {
            var Q0;
            Q0=makeQuery(id+"F38.opExtrude","CAP_FACE",FACE,{"disambiguationData":[OSD([sQuery(id+"F35.wireOp",EDGE,"E127.11.10.0"),sQuery(id+"F35.wireOp",EDGE,"E127.3.11.0"),sQuery(id+"F35.wireOp",EDGE,"E127.4.11.0"),sQuery(id+"F35.wireOp",EDGE,"E127.11.11.0"),sQuery(id+"F35.wireOp",EDGE,"E127.3.12.0"),sQuery(id+"F35.wireOp",EDGE,"E127.4.12.0"),sQuery(id+"F35.wireOp",EDGE,"E127.11.12.0"),sQuery(id+"F35.wireOp",EDGE,"E127.3.13.0"),sQuery(id+"F35.wireOp",EDGE,"E127.4.13.0"),sQuery(id+"F35.wireOp",EDGE,"E175"),sQuery(id+"F35.wireOp",EDGE,"E176")])],"isStart":false});
            var sketch = newSketch(context, id + "F39", { "sketchPlane" : qUnion([Q0])});
            skCircle(sketch, "E177.0", {"center": v(0, 0) * mm, "radius": 314.95 * mm, "construction": true});
            skCircle(sketch, "E178", {"center": v(307.45, 0) * mm, "radius": 7.5 * mm, "construction": true});
            skLineSegment(sketch, "E179.bottom", {"start": v(267.45, -40) * mm, "end": v(347.45, -40) * mm});
            skLineSegment(sketch, "E179.top", {"start": v(267.45, 40) * mm, "end": v(347.45, 40) * mm});
            skLineSegment(sketch, "E179.left", {"start": v(267.45, -40) * mm, "end": v(267.45, 40) * mm});
            skLineSegment(sketch, "E179.right", {"start": v(347.45, -40) * mm, "end": v(347.45, 40) * mm});
            skArc(sketch, "E180.0.0", {"start": v(-385, -300) * mm, "mid": v(-380.6, -310.6) * mm, "end": v(-370, -315) * mm});
            skLineSegment(sketch, "E180.0.1", {"start": v(-370, -315) * mm, "end": v(370, -315) * mm});
            skArc(sketch, "E180.0.2", {"start": v(370, -315) * mm, "mid": v(380.6, -310.6) * mm, "end": v(385, -300) * mm});
            skLineSegment(sketch, "E180.0.3", {"start": v(385, -300) * mm, "end": v(385, 300) * mm});
            skArc(sketch, "E180.0.4", {"start": v(385, 300) * mm, "mid": v(380.6, 310.6) * mm, "end": v(370, 315) * mm});
            skLineSegment(sketch, "E180.0.5", {"start": v(370, 315) * mm, "end": v(-370, 315) * mm});
            skArc(sketch, "E180.0.6", {"start": v(-370, 315) * mm, "mid": v(-380.6, 310.6) * mm, "end": v(-385, 300) * mm});
            skLineSegment(sketch, "E180.0.7", {"start": v(-385, 300) * mm, "end": v(-385, -300) * mm});
            skLineSegment(sketch, "E181.0", {"start": v(-345, -224.78) * mm, "end": v(-345, 224.78) * mm});
            skArc(sketch, "E182.0", {"start": v(-320.5, 236.39) * mm, "mid": v(-336.42, 238.33) * mm, "end": v(-345, 224.78) * mm});
            skLineSegment(sketch, "E183.0", {"start": v(-45.77, 11.6) * mm, "end": v(-320.5, 236.39) * mm});
            skArc(sketch, "E184.0", {"start": v(-262.5, 275) * mm, "mid": v(-276.63, 265.04) * mm, "end": v(-272, 248.4) * mm});
            skLineSegment(sketch, "E185.0", {"start": v(-262.5, 275) * mm, "end": v(262.5, 275) * mm});
            skLineSegment(sketch, "E186.0", {"start": v(-9.5, 33.61) * mm, "end": v(-272, 248.4) * mm});
            skCircle(sketch, "E187.0", {"center": v(-350, 285) * mm, "radius": 15 * mm});
            skCircle(sketch, "E188.0", {"center": v(350, 285) * mm, "radius": 15 * mm});
            skArc(sketch, "E189.0", {"start": v(345, 224.78) * mm, "mid": v(336.42, 238.33) * mm, "end": v(320.5, 236.39) * mm});
            skLineSegment(sketch, "E190.0", {"start": v(345, -224.78) * mm, "end": v(345, 224.78) * mm});
            skLineSegment(sketch, "E191.0", {"start": v(45.77, 11.6) * mm, "end": v(320.5, 236.39) * mm});
            skLineSegment(sketch, "E192.0", {"start": v(9.5, 33.61) * mm, "end": v(272, 248.4) * mm});
            skArc(sketch, "E193.0", {"start": v(272, 248.4) * mm, "mid": v(276.63, 265.04) * mm, "end": v(262.5, 275) * mm});
            skArc(sketch, "E194.0", {"start": v(-9.5, 33.61) * mm, "mid": v(0, 30.22) * mm, "end": v(9.5, 33.61) * mm});
            skArc(sketch, "E195.0", {"start": v(-45.77, -11.6) * mm, "mid": v(-40.27, 0) * mm, "end": v(-45.77, 11.6) * mm});
            skArc(sketch, "E196.0", {"start": v(45.77, 11.6) * mm, "mid": v(40.27, 0) * mm, "end": v(45.77, -11.6) * mm});
            skLineSegment(sketch, "E197.0", {"start": v(-320.5, -236.39) * mm, "end": v(-45.77, -11.6) * mm});
            skLineSegment(sketch, "E198.0", {"start": v(-272, -248.4) * mm, "end": v(-9.5, -33.61) * mm});
            skArc(sketch, "E199.0", {"start": v(9.5, -33.61) * mm, "mid": v(0, -30.22) * mm, "end": v(-9.5, -33.61) * mm});
            skLineSegment(sketch, "E200.0", {"start": v(272, -248.4) * mm, "end": v(9.5, -33.61) * mm});
            skLineSegment(sketch, "E201.0", {"start": v(320.5, -236.39) * mm, "end": v(45.77, -11.6) * mm});
            skLineSegment(sketch, "E202.0", {"start": v(-262.5, -275) * mm, "end": v(262.5, -275) * mm});
            skArc(sketch, "E203.0", {"start": v(262.5, -275) * mm, "mid": v(276.63, -265.04) * mm, "end": v(272, -248.4) * mm});
            skArc(sketch, "E204.0", {"start": v(320.5, -236.39) * mm, "mid": v(336.42, -238.33) * mm, "end": v(345, -224.78) * mm});
            skArc(sketch, "E205.0", {"start": v(-272, -248.4) * mm, "mid": v(-276.63, -265.04) * mm, "end": v(-262.5, -275) * mm});
            skArc(sketch, "E206.0", {"start": v(-345, -224.78) * mm, "mid": v(-336.42, -238.33) * mm, "end": v(-320.5, -236.39) * mm});
            skCircle(sketch, "E207.0", {"center": v(-350, -285) * mm, "radius": 15 * mm});
            skCircle(sketch, "E208.0", {"center": v(350, -285) * mm, "radius": 15 * mm});
            skSolve(sketch);
        }
        {
            var Q0;
            {var subQ0=sQuery(id+"F39.wireOp",EDGE,"E179.left");Q0=makeQuery(id+"F39.imprint","IMPRINT",FACE,{"disambiguationData":[TD([[makeQuery(id+"F39.imprint","IMPRINT",EDGE,{"derivedFrom":subQ0}),-1.0]])]});}
            var Q1;
            {var subQ0=sQuery(id+"F39.wireOp",EDGE,"E190.0");var subQ1=sQuery(id+"F39.wireOp",EDGE,"E179.bottom");var subQ2=makeQuery(id+"F39.imprint","INTERSECT",VERTEX,{"derivedFrom":[subQ1,subQ0]});Q1=makeQuery(id+"F39.imprint","IMPRINT",FACE,{"disambiguationData":[TD([[makeQuery(id+"F39.imprint","IMPRINT",EDGE,{"disambiguationData":[TD([[subQ2,1.0]])],"derivedFrom":subQ1}),1.0]])]});}
            extrude(context, id + "F40", {"entities" : qUnion([Q0, Q1]), "depth" : 100 * mm, "offsetDistance" : 25 * mm});
        }
        {
            var Q0;
            {var subQ49=sQuery(id+"F39.wireOp",EDGE,"E180.0.0");Q0=makeQuery(id+"F39.imprint","IMPRINT",FACE,{"disambiguationData":[TD([[makeQuery(id+"F39.imprint","IMPRINT",EDGE,{"derivedFrom":subQ49}),1.0]])]});}
            var Q1;
            {var subQ28=sQuery(id+"F39.wireOp",EDGE,"E185.0");var subQ30=makeQuery(id+"F38.opExtrude","CAP_EDGE",EDGE,{"disambiguationData":[OSD([sQuery(id+"F35.wireOp",EDGE,"E176")])],"isStart":false});var subQ33=makeQuery(id+"F39.imprint","INTERSECT",VERTEX,{"disambiguationData":[OD(0.0)],"derivedFrom":[subQ30,subQ28]});Q1=makeQuery(id+"F39.imprint","IMPRINT",FACE,{"disambiguationData":[TD([[makeQuery(id+"F39.imprint","IMPRINT",EDGE,{"disambiguationData":[TD([[subQ33,1.0]])],"derivedFrom":subQ30}),-1.0]])]});}
            var Q2;
            {var subQ0=sQuery(id+"F39.wireOp",EDGE,"E185.0");var subQ1=makeQuery(id+"F38.opExtrude","CAP_EDGE",EDGE,{"disambiguationData":[OSD([sQuery(id+"F35.wireOp",EDGE,"E176")])],"isStart":false});var subQ2=makeQuery(id+"F39.imprint","INTERSECT",VERTEX,{"disambiguationData":[OD(0.0)],"derivedFrom":[subQ1,subQ0]});Q2=makeQuery(id+"F39.imprint","IMPRINT",FACE,{"disambiguationData":[TD([[makeQuery(id+"F39.imprint","IMPRINT",EDGE,{"disambiguationData":[TD([[subQ2,-1.0]])],"derivedFrom":subQ0}),1.0]])]});}
            var Q3;
            {var subQ47=sQuery(id+"F39.wireOp",EDGE,"E180.0.2");Q3=makeQuery(id+"F39.imprint","IMPRINT",FACE,{"disambiguationData":[TD([[makeQuery(id+"F39.imprint","IMPRINT",EDGE,{"derivedFrom":subQ47}),1.0]])]});}
            var Q4;
            {var subQ0=sQuery(id+"F39.wireOp",EDGE,"E191.0");var subQ1=makeQuery(id+"F38.opExtrude","CAP_EDGE",EDGE,{"disambiguationData":[OSD([sQuery(id+"F35.wireOp",EDGE,"E176")])],"isStart":false});var subQ2=makeQuery(id+"F39.imprint","INTERSECT",VERTEX,{"derivedFrom":[subQ1,subQ0]});Q4=makeQuery(id+"F39.imprint","IMPRINT",FACE,{"disambiguationData":[TD([[makeQuery(id+"F39.imprint","IMPRINT",EDGE,{"disambiguationData":[TD([[subQ2,-1.0]])],"derivedFrom":subQ1}),-1.0]])]});}
            var Q5;
            {var subQ7=sQuery(id+"F39.wireOp",EDGE,"E194.0");Q5=makeQuery(id+"F39.imprint","IMPRINT",FACE,{"disambiguationData":[TD([[makeQuery(id+"F39.imprint","IMPRINT",EDGE,{"derivedFrom":subQ7}),-1.0]])]});}
            var Q6;
            {var subQ0=sQuery(id+"F39.wireOp",EDGE,"E183.0");var subQ1=makeQuery(id+"F38.opExtrude","CAP_EDGE",EDGE,{"disambiguationData":[OSD([sQuery(id+"F35.wireOp",EDGE,"E176")])],"isStart":false});var subQ2=makeQuery(id+"F39.imprint","INTERSECT",VERTEX,{"derivedFrom":[subQ1,subQ0]});Q6=makeQuery(id+"F39.imprint","IMPRINT",FACE,{"disambiguationData":[TD([[makeQuery(id+"F39.imprint","IMPRINT",EDGE,{"disambiguationData":[TD([[subQ2,1.0]])],"derivedFrom":subQ1}),-1.0]])]});}
            var Q7;
            {var subQ0=sQuery(id+"F35.wireOp",EDGE,"E127.4.11.0");var subQ1=makeQuery(id+"F38.opExtrude","CAP_EDGE",EDGE,{"disambiguationData":[OSD([subQ0])],"isStart":false});Q7=makeQuery(id+"F39.imprint","IMPRINT",FACE,{"disambiguationData":[TD([[makeQuery(id+"F39.imprint","IMPRINT",EDGE,{"derivedFrom":subQ1}),1.0]])]});}
            var Q8;
            {var subQ0=sQuery(id+"F39.wireOp",EDGE,"E202.0");var subQ28=makeQuery(id+"F38.opExtrude","CAP_EDGE",EDGE,{"disambiguationData":[OSD([sQuery(id+"F35.wireOp",EDGE,"E176")])],"isStart":false});var subQ29=makeQuery(id+"F39.imprint","INTERSECT",VERTEX,{"disambiguationData":[OD(0.0)],"derivedFrom":[subQ28,subQ0]});Q8=makeQuery(id+"F39.imprint","IMPRINT",FACE,{"disambiguationData":[TD([[makeQuery(id+"F39.imprint","IMPRINT",EDGE,{"disambiguationData":[TD([[subQ29,-1.0]])],"derivedFrom":subQ28}),-1.0]])]});}
            var Q9;
            {var subQ0=sQuery(id+"F39.wireOp",EDGE,"E202.0");var subQ1=makeQuery(id+"F38.opExtrude","CAP_EDGE",EDGE,{"disambiguationData":[OSD([sQuery(id+"F35.wireOp",EDGE,"E176")])],"isStart":false});var subQ2=makeQuery(id+"F39.imprint","INTERSECT",VERTEX,{"disambiguationData":[OD(0.0)],"derivedFrom":[subQ1,subQ0]});Q9=makeQuery(id+"F39.imprint","IMPRINT",FACE,{"disambiguationData":[TD([[makeQuery(id+"F39.imprint","IMPRINT",EDGE,{"disambiguationData":[TD([[subQ2,-1.0]])],"derivedFrom":subQ0}),-1.0]])]});}
            var Q10;
            {var subQ0=sQuery(id+"F39.wireOp",EDGE,"E200.0");var subQ28=makeQuery(id+"F38.opExtrude","CAP_EDGE",EDGE,{"disambiguationData":[OSD([sQuery(id+"F35.wireOp",EDGE,"E176")])],"isStart":false});var subQ29=makeQuery(id+"F39.imprint","INTERSECT",VERTEX,{"derivedFrom":[subQ28,subQ0]});Q10=makeQuery(id+"F39.imprint","IMPRINT",FACE,{"disambiguationData":[TD([[makeQuery(id+"F39.imprint","IMPRINT",EDGE,{"disambiguationData":[TD([[subQ29,-1.0]])],"derivedFrom":subQ28}),-1.0]])]});}
            var Q11;
            {var subQ30=sQuery(id+"F39.wireOp",EDGE,"E179.right");Q11=makeQuery(id+"F39.imprint","IMPRINT",FACE,{"disambiguationData":[TD([[makeQuery(id+"F39.imprint","IMPRINT",EDGE,{"derivedFrom":subQ30}),-1.0]])]});}
            extrude(context, id + "F41", {"entities" : qUnion([Q0, Q1, Q2, Q3, Q4, Q5, Q6, Q7, Q8, Q9, Q10, Q11]), "depth" : 15 * mm, "offsetDistance" : 25 * mm});
        }
    });
